FCSTD DOCUMENT  (FreeCAD 1.0R39109 (Git))
Label: 00_tool_cabinet_assembly
License: All rights reserved
LicenseURL: http://en.wikipedia.org/wiki/All_rights_reserved
objects: App::Link×62, App::FeaturePython×28, TechDraw::DrawViewDimension×15, Assembly::AssemblyLink×10, TechDraw::DrawProjGroupItem×5, TechDraw::DrawSVGTemplate×1, Assembly::JointGroup×1, Assembly::AssemblyObject×1, TechDraw::DrawProjGroup×1, TechDraw::DrawViewSection×1, TechDraw::DrawPage×1
note: 26 computed .brp shape members not serialized (recipe doc carries the construction recipe); baked Part::Feature solids carry a one-line shape summary decoded from their .brp
EXTERNAL_REF file=80_base_assembly.FCStd obj=Assembly
EXTERNAL_REF file=80_base_assembly.FCStd obj=Body
EXTERNAL_REF file=80_base_assembly.FCStd obj=Body001
EXTERNAL_REF file=80_base_assembly.FCStd obj=Body002
EXTERNAL_REF file=80_base_assembly.FCStd obj=Body003
EXTERNAL_REF file=10_drawer_96mm_assembly.FCStd obj=Assembly
EXTERNAL_REF file=10_drawer_96mm_assembly.FCStd obj=Body
EXTERNAL_REF file=10_drawer_96mm_assembly.FCStd obj=Body001
EXTERNAL_REF file=10_drawer_96mm_assembly.FCStd obj=Body002
EXTERNAL_REF file=10_drawer_96mm_assembly.FCStd obj=Body003
EXTERNAL_REF file=10_drawer_96mm_assembly.FCStd obj=Body004
EXTERNAL_REF file=10_drawer_96mm_assembly.FCStd obj=Body005
EXTERNAL_REF file=70_drawer_box_assembly.FCStd obj=Assembly
EXTERNAL_REF file=70_drawer_box_assembly.FCStd obj=Body
EXTERNAL_REF file=70_drawer_box_assembly.FCStd obj=Body003
EXTERNAL_REF file=70_drawer_box_assembly.FCStd obj=Body004
EXTERNAL_REF file=70_drawer_box_assembly.FCStd obj=Body005
EXTERNAL_REF file=70_drawer_box_assembly.FCStd obj=KV1_45_H45_L____SC
EXTERNAL_REF file=70_drawer_box_assembly.FCStd obj=Body007
EXTERNAL_REF file=70_drawer_box_assembly.FCStd obj=Assembly001
EXTERNAL_REF file=70_drawer_box_assembly.FCStd obj=KV1_45_H45_L____SC001
EXTERNAL_REF file=70_drawer_box_assembly.FCStd obj=KV1_45_H45_L____SC002
EXTERNAL_REF file=70_drawer_box_assembly.FCStd obj=KV1_45_H45_L____SC003

FEATURE [TechDraw::DrawSVGTemplate] Template
  Height = 210
  Orientation = 1
  Template = C:/Program Files/FreeCAD 1.0/data/Mod/TechDraw/Templates/Default_Template_A4_Landscape.svg
  Width = 297
FEATURE [App::Link] Body
  LinkedObject = -> <external 80_base_assembly.FCStd>#Body
FEATURE [App::Link] Body001
  LinkPlacement = pos=(-1.91e-14,1.232e-13,375) rot=(1,0,0;3.14159rad)
  LinkedObject = -> <external 80_base_assembly.FCStd>#Body001
  Placement = pos=(-1.91e-14,1.232e-13,375) rot=(1,0,0;3.14159rad)
FEATURE [App::Link] Body002
  LinkPlacement = pos=(-262.5,9.58e-14,187.5) rot=(0.707107,0,0.707107;3.14159rad)
  LinkedObject = -> <external 80_base_assembly.FCStd>#Body002
  Placement = pos=(-262.5,9.58e-14,187.5) rot=(0.707107,0,0.707107;3.14159rad)
FEATURE [App::Link] Body003
  LinkPlacement = pos=(244.5,3.53e-14,187.5) rot=(0,1,0;1.5708rad)
  LinkedObject = -> <external 80_base_assembly.FCStd>#Body003
  Placement = pos=(244.5,3.53e-14,187.5) rot=(0,1,0;1.5708rad)
FEATURE [Assembly::AssemblyLink] Assembly001
  Group = -> [Body,Body001,Body002,Body003]
  LinkedObject = -> <external 80_base_assembly.FCStd>#Assembly
  Origin = -> Origin001
  Rigid = true
FEATURE [App::FeaturePython] GroundedJoint  # Assembly grounded joint (typed FeaturePython)
  ObjectToGround = -> Assembly001
FEATURE [App::Link] Body004
  LinkedObject = -> <external 10_drawer_96mm_assembly.FCStd>#Body
FEATURE [App::Link] Body005
  LinkPlacement = pos=(-0.0692255,177.5,34.4999) rot=(0.999999,-0.001116,0.001116;1.5708rad)
  LinkedObject = -> <external 10_drawer_96mm_assembly.FCStd>#Body001
  Placement = pos=(-0.0692255,177.5,34.4999) rot=(0.999999,-0.001116,0.001116;1.5708rad)
FEATURE [App::Link] Body006
  LinkPlacement = pos=(2.3e-15,-177.5,34) rot=(0,0.707107,0.707107;3.14159rad)
  LinkedObject = -> <external 10_drawer_96mm_assembly.FCStd>#Body002
  Placement = pos=(2.3e-15,-177.5,34) rot=(0,0.707107,0.707107;3.14159rad)
FEATURE [App::Link] Body007
  LinkPlacement = pos=(-231.5,-4.06e-14,34) rot=(0.57735,0.57735,0.57735;2.0944rad)
  LinkedObject = -> <external 10_drawer_96mm_assembly.FCStd>#Body003
  Placement = pos=(-231.5,-4.06e-14,34) rot=(0.57735,0.57735,0.57735;2.0944rad)
FEATURE [App::Link] Body008
  LinkPlacement = pos=(231.5,-6.4e-15,34) rot=(0.57735,-0.57735,-0.57735;2.0944rad)
  LinkedObject = -> <external 10_drawer_96mm_assembly.FCStd>#Body004
  Placement = pos=(231.5,-6.4e-15,34) rot=(0.57735,-0.57735,-0.57735;2.0944rad)
FEATURE [App::Link] Body009
  LinkPlacement = pos=(2.5e-15,-177.5,33.5) rot=(0,-0.707107,0.707107;3.14159rad)
  LinkedObject = -> <external 10_drawer_96mm_assembly.FCStd>#Body005
  Placement = pos=(2.5e-15,-177.5,33.5) rot=(0,-0.707107,0.707107;3.14159rad)
FEATURE [Assembly::AssemblyLink] Assembly002
  Group = -> [Body004,Body005,Body006,Body007,Body008,Body009]
  LinkedObject = -> <external 10_drawer_96mm_assembly.FCStd>#Assembly
  Origin = -> Origin002
  Placement = pos=(-8.81e-14,-59,174.5) rot=(1,0,0;1.5708rad)
  Rigid = true
FEATURE [App::Link] Body010
  LinkPlacement = pos=(0,0,0) rot=(0,0,1;3.14159rad)
  LinkedObject = -> <external 70_drawer_box_assembly.FCStd>#Body
  Placement = pos=(0,0,0) rot=(0,0,1;3.14159rad)
FEATURE [App::Link] Body011
  LinkPlacement = pos=(-1.536e-13,-1.625e-13,-771) rot=(1,0,0;3.14159rad)
  LinkedObject = -> <external 70_drawer_box_assembly.FCStd>#Body003
  Placement = pos=(-1.536e-13,-1.625e-13,-771) rot=(1,0,0;3.14159rad)
FEATURE [App::Link] Body012
  LinkPlacement = pos=(-262.5,7.5,-385.5) rot=(0,1,0;1.5708rad)
  LinkedObject = -> <external 70_drawer_box_assembly.FCStd>#Body004
  Placement = pos=(-262.5,7.5,-385.5) rot=(0,1,0;1.5708rad)
FEATURE [App::Link] Body013
  LinkPlacement = pos=(244.5,7.5,-385.5) rot=(0,1,0;1.5708rad)
  LinkedObject = -> <external 70_drawer_box_assembly.FCStd>#Body005
  Placement = pos=(244.5,7.5,-385.5) rot=(0,1,0;1.5708rad)
FEATURE [App::Link] KV1_45_H45_L____SC  label="KV1-45-H45-L...-SC"
  LinkPlacement = pos=(238.45,-31,-41.5) rot=(0,-0.707107,0.707107;3.14159rad)
  LinkedObject = -> <external 70_drawer_box_assembly.FCStd>#KV1_45_H45_L____SC
  Placement = pos=(238.45,-31,-41.5) rot=(0,-0.707107,0.707107;3.14159rad)
FEATURE [App::Link] Body014
  LinkPlacement = pos=(-8.19e-14,196.5,-386) rot=(0,-0.707107,0.707107;3.14159rad)
  LinkedObject = -> <external 70_drawer_box_assembly.FCStd>#Body007
  Placement = pos=(-8.19e-14,196.5,-386) rot=(0,-0.707107,0.707107;3.14159rad)
FEATURE [App::FeaturePython] Joint  label="Distance"  # Assembly joint (typed FeaturePython)
  Activated = true
  AngleMax = 0
  AngleMin = 0
  Detach1 = false
  Detach2 = false
  Distance = 0
  Distance2 = 0
  EnableAngleMax = false
  EnableAngleMin = false
  EnableLengthMax = false
  EnableLengthMin = false
  JointType = 5 (Distance)
  LengthMax = 0
  LengthMin = 0
  Placement1 = pos=(4.7e-15,6.1e-15,18) rot=(0,0,1;0rad)
  Placement2 = pos=(0,25,9) rot=(-1,0,0;1.5708rad)
  Reference1 = -> Assembly [Assembly003.Body010.Face5,Assembly003.Body010.Face5]
  Reference2 = -> Assembly [Assembly001.Body002.Face1,Assembly001.Body002.Vertex3]
FEATURE [App::FeaturePython] Joint001  label="Distance001"  # Assembly joint (typed FeaturePython)
  Activated = true
  AngleMax = 0
  AngleMin = 0
  Detach1 = false
  Detach2 = false
  Distance = 0
  Distance2 = 0
  EnableAngleMax = false
  EnableAngleMin = false
  EnableLengthMax = false
  EnableLengthMin = false
  JointType = 5 (Distance)
  LengthMax = 0
  LengthMin = 0
  Placement1 = pos=(262.5,2.2e-15,9) rot=(-0.57735,0.57735,-0.57735;2.0944rad)
  Placement2 = pos=(0,-3e-16,18) rot=(0,0,1;0rad)
  Reference1 = -> Assembly [Assembly003.Body010.Face3,Assembly003.Body010.Vertex4]
  Reference2 = -> Assembly [Assembly001.Body003.Face6,Assembly001.Body003.Face6]
FEATURE [App::FeaturePython] Joint002  label="Distance002"  # Assembly joint (typed FeaturePython)
  Activated = true
  AngleMax = 0
  AngleMin = 0
  Detach1 = false
  Detach2 = false
  Distance = 0
  Distance2 = 0
  EnableAngleMax = false
  EnableAngleMin = false
  EnableLengthMax = false
  EnableLengthMin = false
  JointType = 5 (Distance)
  LengthMax = 0
  LengthMin = 0
  Placement1 = pos=(-1e-14,0,0) rot=(0,0,1;0rad)
  Placement2 = pos=(-2e-16,-196.5,9) rot=(0,0.707107,-0.707107;3.14159rad)
  Reference1 = -> Assembly [Assembly001.Body001.Face5,Assembly001.Body001.Vertex5]
  Reference2 = -> Assembly [Assembly003.Body010.Face6,Assembly003.Body010.Vertex7]
FEATURE [App::FeaturePython] Joint003  label="Distance003"  # Assembly joint (typed FeaturePython)
  Activated = true
  AngleMax = 0
  AngleMin = 0
  Detach1 = false
  Detach2 = false
  Distance = 3
  Distance2 = 0
  EnableAngleMax = false
  EnableAngleMin = false
  EnableLengthMax = false
  EnableLengthMin = false
  JointType = 5 (Distance)
  LengthMax = 0
  LengthMin = 0
  Placement1 = pos=(-6.6e-15,46.5,7.5) rot=(1,0,0;4.71239rad)
  Placement2 = pos=(4.7e-15,3.01501,0) rot=(0,0,1;0rad)
  Reference1 = -> Assembly [Assembly002.Body009.Face1,Assembly002.Body009.Face1]
  Reference2 = -> Assembly [Assembly003.Body010.Face4,Assembly003.Body010.Face4]
FEATURE [App::FeaturePython] Joint004  label="Distance004"  # Assembly joint (typed FeaturePython)
  Activated = true
  AngleMax = 0
  AngleMin = 0
  Detach1 = false
  Detach2 = false
  Distance = 0
  Distance2 = 0
  EnableAngleMax = false
  EnableAngleMin = false
  EnableLengthMax = false
  EnableLengthMin = false
  JointType = 5 (Distance)
  LengthMax = 0
  LengthMin = 0
  Placement1 = pos=(3.9e-15,0,0) rot=(0,0,1;0rad)
  Placement2 = pos=(0,-189,9) rot=(0,-0.707107,0.707107;3.14159rad)
  Reference1 = -> Assembly [Assembly002.Body009.Face5,Assembly002.Body009.Vertex1]
  Reference2 = -> Assembly [Assembly003.Body012.Face10,Assembly003.Body012.Vertex10]
FEATURE [App::FeaturePython] Joint005  label="Distance005"  # Assembly joint (typed FeaturePython)
  Activated = true
  AngleMax = 0
  AngleMin = 0
  Detach1 = false
  Detach2 = false
  Distance = 2
  Distance2 = 0
  EnableAngleMax = false
  EnableAngleMin = false
  EnableLengthMax = false
  EnableLengthMin = false
  JointType = 5 (Distance)
  LengthMax = 0
  LengthMin = 0
  Placement1 = pos=(260.5,-7.1e-15,7.5) rot=(-0.57735,0.57735,-0.57735;2.0944rad)
  Placement2 = pos=(0,3.6e-15,18) rot=(0,0,1;0rad)
  Reference1 = -> Assembly [Assembly002.Body009.Face2,Assembly002.Body009.Face2]
  Reference2 = -> Assembly [Assembly003.Body013.Face5,Assembly003.Body013.Vertex10]
FEATURE [App::Link] Assembly004
  LinkedObject = -> <external 70_drawer_box_assembly.FCStd>#Assembly001
FEATURE [App::Link] KV1_45_H45_L____SC001  label="KV1-45-H45-L...-SC001"
  LinkPlacement = pos=(239.05,-31,-233.479) rot=(-0.001394,0.707106,-0.707106;3.14438rad)
  LinkedObject = -> <external 70_drawer_box_assembly.FCStd>#KV1_45_H45_L____SC001
  Placement = pos=(239.05,-31,-233.479) rot=(-0.001394,0.707106,-0.707106;3.14438rad)
FEATURE [App::Link] KV1_45_H45_L____SC002  label="KV1-45-H45-L...-SC002"
  LinkPlacement = pos=(238.45,-31,-137.5) rot=(0,-0.707107,0.707107;3.14159rad)
  LinkedObject = -> <external 70_drawer_box_assembly.FCStd>#KV1_45_H45_L____SC002
  Placement = pos=(238.45,-31,-137.5) rot=(0,-0.707107,0.707107;3.14159rad)
FEATURE [App::Link] KV1_45_H45_L____SC003  label="KV1-45-H45-L...-SC003"
  LinkPlacement = pos=(238.71,-31.0451,-329.552) rot=(0.002831,-0.706671,0.707537;3.14726rad)
  LinkedObject = -> <external 70_drawer_box_assembly.FCStd>#KV1_45_H45_L____SC003
  Placement = pos=(238.71,-31.0451,-329.552) rot=(0.002831,-0.706671,0.707537;3.14726rad)
FEATURE [Assembly::AssemblyLink] Assembly003
  Group = -> [Body010,Body011,Body012,Body013,KV1_45_H45_L____SC,Body014,Assembly004,KV1_45_H45_L____SC001,KV1_45_H45_L____SC002,KV1_45_H45_L____SC003]
  LinkedObject = -> <external 70_drawer_box_assembly.FCStd>#Assembly
  Origin = -> Origin003
  Placement = pos=(-1.92e-14,-43,178.5) rot=(0,0.707107,0.707107;3.14159rad)
  Rigid = true
FEATURE [App::Link] Body015
  LinkedObject = -> <external 10_drawer_96mm_assembly.FCStd>#Body
FEATURE [App::Link] Body016
  LinkPlacement = pos=(-0.0692255,177.5,34.4999) rot=(0.999999,-0.001116,0.001116;1.5708rad)
  LinkedObject = -> <external 10_drawer_96mm_assembly.FCStd>#Body001
  Placement = pos=(-0.0692255,177.5,34.4999) rot=(0.999999,-0.001116,0.001116;1.5708rad)
FEATURE [App::Link] Body017
  LinkPlacement = pos=(2.3e-15,-177.5,34) rot=(0,0.707107,0.707107;3.14159rad)
  LinkedObject = -> <external 10_drawer_96mm_assembly.FCStd>#Body002
  Placement = pos=(2.3e-15,-177.5,34) rot=(0,0.707107,0.707107;3.14159rad)
FEATURE [App::Link] Body018
  LinkPlacement = pos=(-231.5,-4.06e-14,34) rot=(0.57735,0.57735,0.57735;2.0944rad)
  LinkedObject = -> <external 10_drawer_96mm_assembly.FCStd>#Body003
  Placement = pos=(-231.5,-4.06e-14,34) rot=(0.57735,0.57735,0.57735;2.0944rad)
FEATURE [App::Link] Body019
  LinkPlacement = pos=(231.5,-6.4e-15,34) rot=(0.57735,-0.57735,-0.57735;2.0944rad)
  LinkedObject = -> <external 10_drawer_96mm_assembly.FCStd>#Body004
  Placement = pos=(231.5,-6.4e-15,34) rot=(0.57735,-0.57735,-0.57735;2.0944rad)
FEATURE [App::Link] Body020
  LinkPlacement = pos=(2.5e-15,-177.5,33.5) rot=(0,-0.707107,0.707107;3.14159rad)
  LinkedObject = -> <external 10_drawer_96mm_assembly.FCStd>#Body005
  Placement = pos=(2.5e-15,-177.5,33.5) rot=(0,-0.707107,0.707107;3.14159rad)
FEATURE [Assembly::AssemblyLink] Assembly005
  Group = -> [Body015,Body016,Body017,Body018,Body019,Body020]
  LinkedObject = -> <external 10_drawer_96mm_assembly.FCStd>#Assembly
  Origin = -> Origin004
  Placement = pos=(-9.65e-14,-155,174.5) rot=(1,0,0;1.5708rad)
  Rigid = true
FEATURE [App::FeaturePython] Joint006  label="Distance006"  # Assembly joint (typed FeaturePython)
  Activated = true
  AngleMax = 0
  AngleMin = 0
  Detach1 = false
  Detach2 = false
  Distance = 3
  Distance2 = 0
  EnableAngleMax = false
  EnableAngleMin = false
  EnableLengthMax = false
  EnableLengthMin = false
  JointType = 5 (Distance)
  LengthMax = 0
  LengthMin = 0
  Placement1 = pos=(-6.6e-15,46.5,7.5) rot=(1,0,0;4.71239rad)
  Placement2 = pos=(1.03e-14,-46.5,7.5) rot=(0,0.707107,-0.707107;3.14159rad)
  Reference1 = -> Assembly [Assembly005.Body020.Face1,Assembly005.Body020.Face1]
  Reference2 = -> Assembly [Assembly002.Body009.Face3,Assembly002.Body009.Vertex5]
FEATURE [App::FeaturePython] Joint007  label="Distance007"  # Assembly joint (typed FeaturePython)
  Activated = true
  AngleMax = 0
  AngleMin = 0
  Detach1 = false
  Detach2 = false
  Distance = 0
  Distance2 = 0
  EnableAngleMax = false
  EnableAngleMin = false
  EnableLengthMax = false
  EnableLengthMin = false
  JointType = 5 (Distance)
  LengthMax = 0
  LengthMin = 0
  Placement1 = pos=(0,-189,9) rot=(0,-0.707107,0.707107;3.14159rad)
  Placement2 = pos=(3.9e-15,0,0) rot=(0,0,1;0rad)
  Reference1 = -> Assembly [Assembly003.Body012.Face10,Assembly003.Body012.Vertex10]
  Reference2 = -> Assembly [Assembly005.Body020.Face5,Assembly005.Body020.Vertex1]
FEATURE [App::FeaturePython] Joint008  label="Distance008"  # Assembly joint (typed FeaturePython)
  Activated = true
  AngleMax = 0
  AngleMin = 0
  Detach1 = false
  Detach2 = false
  Distance = 2
  Distance2 = 0
  EnableAngleMax = false
  EnableAngleMin = false
  EnableLengthMax = false
  EnableLengthMin = false
  JointType = 5 (Distance)
  LengthMax = 0
  LengthMin = 0
  Placement1 = pos=(-260.5,0,7.5) rot=(0.57735,0.57735,-0.57735;4.18879rad)
  Placement2 = pos=(0,-4.4e-15,0) rot=(0,0,1;0rad)
  Reference1 = -> Assembly [Assembly005.Body020.Face4,Assembly005.Body020.Face4]
  Reference2 = -> Assembly [Assembly003.Body012.Face4,Assembly003.Body012.Vertex5]
FEATURE [App::Link] Body021
  LinkedObject = -> <external 10_drawer_96mm_assembly.FCStd>#Body
FEATURE [App::Link] Body022
  LinkPlacement = pos=(-0.0692255,177.5,34.4999) rot=(0.999999,-0.001116,0.001116;1.5708rad)
  LinkedObject = -> <external 10_drawer_96mm_assembly.FCStd>#Body001
  Placement = pos=(-0.0692255,177.5,34.4999) rot=(0.999999,-0.001116,0.001116;1.5708rad)
FEATURE [App::Link] Body023
  LinkPlacement = pos=(2.3e-15,-177.5,34) rot=(0,0.707107,0.707107;3.14159rad)
  LinkedObject = -> <external 10_drawer_96mm_assembly.FCStd>#Body002
  Placement = pos=(2.3e-15,-177.5,34) rot=(0,0.707107,0.707107;3.14159rad)
FEATURE [App::Link] Body024
  LinkPlacement = pos=(-231.5,-4.06e-14,34) rot=(0.57735,0.57735,0.57735;2.0944rad)
  LinkedObject = -> <external 10_drawer_96mm_assembly.FCStd>#Body003
  Placement = pos=(-231.5,-4.06e-14,34) rot=(0.57735,0.57735,0.57735;2.0944rad)
FEATURE [App::Link] Body025
  LinkPlacement = pos=(231.5,-6.4e-15,34) rot=(0.57735,-0.57735,-0.57735;2.0944rad)
  LinkedObject = -> <external 10_drawer_96mm_assembly.FCStd>#Body004
  Placement = pos=(231.5,-6.4e-15,34) rot=(0.57735,-0.57735,-0.57735;2.0944rad)
FEATURE [App::Link] Body026
  LinkPlacement = pos=(2.5e-15,-177.5,33.5) rot=(0,-0.707107,0.707107;3.14159rad)
  LinkedObject = -> <external 10_drawer_96mm_assembly.FCStd>#Body005
  Placement = pos=(2.5e-15,-177.5,33.5) rot=(0,-0.707107,0.707107;3.14159rad)
FEATURE [Assembly::AssemblyLink] Assembly006
  Group = -> [Body021,Body022,Body023,Body024,Body025,Body026]
  LinkedObject = -> <external 10_drawer_96mm_assembly.FCStd>#Assembly
  Origin = -> Origin005
  Placement = pos=(2.04e-14,-347,174.5) rot=(1,0,0;1.5708rad)
  Rigid = true
FEATURE [App::Link] Body027
  LinkedObject = -> <external 10_drawer_96mm_assembly.FCStd>#Body
FEATURE [App::Link] Body028
  LinkPlacement = pos=(-0.0692255,177.5,34.4999) rot=(0.999999,-0.001116,0.001116;1.5708rad)
  LinkedObject = -> <external 10_drawer_96mm_assembly.FCStd>#Body001
  Placement = pos=(-0.0692255,177.5,34.4999) rot=(0.999999,-0.001116,0.001116;1.5708rad)
FEATURE [App::Link] Body029
  LinkPlacement = pos=(2.3e-15,-177.5,34) rot=(0,0.707107,0.707107;3.14159rad)
  LinkedObject = -> <external 10_drawer_96mm_assembly.FCStd>#Body002
  Placement = pos=(2.3e-15,-177.5,34) rot=(0,0.707107,0.707107;3.14159rad)
FEATURE [App::Link] Body030
  LinkPlacement = pos=(-231.5,-4.06e-14,34) rot=(0.57735,0.57735,0.57735;2.0944rad)
  LinkedObject = -> <external 10_drawer_96mm_assembly.FCStd>#Body003
  Placement = pos=(-231.5,-4.06e-14,34) rot=(0.57735,0.57735,0.57735;2.0944rad)
FEATURE [App::Link] Body031
  LinkPlacement = pos=(231.5,-6.4e-15,34) rot=(0.57735,-0.57735,-0.57735;2.0944rad)
  LinkedObject = -> <external 10_drawer_96mm_assembly.FCStd>#Body004
  Placement = pos=(231.5,-6.4e-15,34) rot=(0.57735,-0.57735,-0.57735;2.0944rad)
FEATURE [App::Link] Body032
  LinkPlacement = pos=(2.5e-15,-177.5,33.5) rot=(0,-0.707107,0.707107;3.14159rad)
  LinkedObject = -> <external 10_drawer_96mm_assembly.FCStd>#Body005
  Placement = pos=(2.5e-15,-177.5,33.5) rot=(0,-0.707107,0.707107;3.14159rad)
FEATURE [Assembly::AssemblyLink] Assembly007
  Group = -> [Body027,Body028,Body029,Body030,Body031,Body032]
  LinkedObject = -> <external 10_drawer_96mm_assembly.FCStd>#Assembly
  Origin = -> Origin006
  Placement = pos=(3.41e-14,-251,174.5) rot=(1,0,0;1.5708rad)
  Rigid = true
FEATURE [App::FeaturePython] Joint009  label="Distance009"  # Assembly joint (typed FeaturePython)
  Activated = true
  AngleMax = 0
  AngleMin = 0
  Detach1 = false
  Detach2 = false
  Distance = 3
  Distance2 = 0
  EnableAngleMax = false
  EnableAngleMin = false
  EnableLengthMax = false
  EnableLengthMin = false
  JointType = 5 (Distance)
  LengthMax = 0
  LengthMin = 0
  Placement1 = pos=(-6.6e-15,46.5,7.5) rot=(1,0,0;4.71239rad)
  Placement2 = pos=(1.03e-14,-46.5,7.5) rot=(0,0.707107,-0.707107;3.14159rad)
  Reference1 = -> Assembly [Assembly007.Body032.Face1,Assembly007.Body032.Vertex3]
  Reference2 = -> Assembly [Assembly005.Body020.Face3,Assembly005.Body020.Face3]
FEATURE [App::FeaturePython] Joint010  label="Distance010"  # Assembly joint (typed FeaturePython)
  Activated = true
  AngleMax = 0
  AngleMin = 0
  Detach1 = false
  Detach2 = false
  Distance = 0
  Distance2 = 0
  EnableAngleMax = false
  EnableAngleMin = false
  EnableLengthMax = false
  EnableLengthMin = false
  JointType = 5 (Distance)
  LengthMax = 0
  LengthMin = 0
  Placement1 = pos=(0,-189,9) rot=(0,-0.707107,0.707107;3.14159rad)
  Placement2 = pos=(3.9e-15,0,0) rot=(0,0,1;0rad)
  Reference1 = -> Assembly [Assembly003.Body012.Face10,Assembly003.Body012.Face10]
  Reference2 = -> Assembly [Assembly007.Body032.Face5,Assembly007.Body032.Vertex7]
FEATURE [App::FeaturePython] Joint011  label="Distance011"  # Assembly joint (typed FeaturePython)
  Activated = true
  AngleMax = 0
  AngleMin = 0
  Detach1 = false
  Detach2 = false
  Distance = 2
  Distance2 = 0
  EnableAngleMax = false
  EnableAngleMin = false
  EnableLengthMax = false
  EnableLengthMin = false
  JointType = 5 (Distance)
  LengthMax = 0
  LengthMin = 0
  Placement1 = pos=(-260.5,0,7.5) rot=(0.57735,0.57735,-0.57735;4.18879rad)
  Placement2 = pos=(0,-4.4e-15,0) rot=(0,0,1;0rad)
  Reference1 = -> Assembly [Assembly007.Body032.Face4,Assembly007.Body032.Face4]
  Reference2 = -> Assembly [Assembly003.Body012.Face4,Assembly003.Body012.Face4]
FEATURE [App::FeaturePython] Joint012  label="Distance012"  # Assembly joint (typed FeaturePython)
  Activated = true
  AngleMax = 0
  AngleMin = 0
  Detach1 = false
  Detach2 = false
  Distance = 3
  Distance2 = 0
  EnableAngleMax = false
  EnableAngleMin = false
  EnableLengthMax = false
  EnableLengthMin = false
  JointType = 5 (Distance)
  LengthMax = 0
  LengthMin = 0
  Placement1 = pos=(-6.6e-15,46.5,7.5) rot=(1,0,0;4.71239rad)
  Placement2 = pos=(1.03e-14,-46.5,7.5) rot=(0,0.707107,-0.707107;3.14159rad)
  Reference1 = -> Assembly [Assembly006.Body026.Face1,Assembly006.Body026.Vertex1]
  Reference2 = -> Assembly [Assembly007.Body032.Face3,Assembly007.Body032.Face3]
FEATURE [App::FeaturePython] Joint013  label="Distance013"  # Assembly joint (typed FeaturePython)
  Activated = true
  AngleMax = 0
  AngleMin = 0
  Detach1 = false
  Detach2 = false
  Distance = 0
  Distance2 = 0
  EnableAngleMax = false
  EnableAngleMin = false
  EnableLengthMax = false
  EnableLengthMin = false
  JointType = 5 (Distance)
  LengthMax = 0
  LengthMin = 0
  Placement1 = pos=(3.9e-15,0,0) rot=(0,0,1;0rad)
  Placement2 = pos=(0,-189,9) rot=(0,-0.707107,0.707107;3.14159rad)
  Reference1 = -> Assembly [Assembly006.Body026.Face5,Assembly006.Body026.Vertex1]
  Reference2 = -> Assembly [Assembly003.Body012.Face10,Assembly003.Body012.Face10]
FEATURE [App::FeaturePython] Joint014  label="Distance014"  # Assembly joint (typed FeaturePython)
  Activated = true
  AngleMax = 0
  AngleMin = 0
  Detach1 = false
  Detach2 = false
  Distance = 2
  Distance2 = 0
  EnableAngleMax = false
  EnableAngleMin = false
  EnableLengthMax = false
  EnableLengthMin = false
  JointType = 5 (Distance)
  LengthMax = 0
  LengthMin = 0
  Placement1 = pos=(-260.5,0,7.5) rot=(0.57735,0.57735,-0.57735;4.18879rad)
  Placement2 = pos=(0,-4.4e-15,0) rot=(0,0,1;0rad)
  Reference1 = -> Assembly [Assembly006.Body026.Face4,Assembly006.Body026.Face4]
  Reference2 = -> Assembly [Assembly003.Body012.Face4,Assembly003.Body012.Face4]
FEATURE [App::Link] Body033
  LinkedObject = -> <external 10_drawer_96mm_assembly.FCStd>#Body
FEATURE [App::Link] Body034
  LinkPlacement = pos=(-0.0692255,177.5,34.4999) rot=(0.999999,-0.001116,0.001116;1.5708rad)
  LinkedObject = -> <external 10_drawer_96mm_assembly.FCStd>#Body001
  Placement = pos=(-0.0692255,177.5,34.4999) rot=(0.999999,-0.001116,0.001116;1.5708rad)
FEATURE [App::Link] Body035
  LinkPlacement = pos=(2.3e-15,-177.5,34) rot=(0,0.707107,0.707107;3.14159rad)
  LinkedObject = -> <external 10_drawer_96mm_assembly.FCStd>#Body002
  Placement = pos=(2.3e-15,-177.5,34) rot=(0,0.707107,0.707107;3.14159rad)
FEATURE [App::Link] Body036
  LinkPlacement = pos=(-231.5,-4.06e-14,34) rot=(0.57735,0.57735,0.57735;2.0944rad)
  LinkedObject = -> <external 10_drawer_96mm_assembly.FCStd>#Body003
  Placement = pos=(-231.5,-4.06e-14,34) rot=(0.57735,0.57735,0.57735;2.0944rad)
FEATURE [App::Link] Body037
  LinkPlacement = pos=(231.5,-6.4e-15,34) rot=(0.57735,-0.57735,-0.57735;2.0944rad)
  LinkedObject = -> <external 10_drawer_96mm_assembly.FCStd>#Body004
  Placement = pos=(231.5,-6.4e-15,34) rot=(0.57735,-0.57735,-0.57735;2.0944rad)
FEATURE [App::Link] Body038
  LinkPlacement = pos=(2.5e-15,-177.5,33.5) rot=(0,-0.707107,0.707107;3.14159rad)
  LinkedObject = -> <external 10_drawer_96mm_assembly.FCStd>#Body005
  Placement = pos=(2.5e-15,-177.5,33.5) rot=(0,-0.707107,0.707107;3.14159rad)
FEATURE [Assembly::AssemblyLink] Assembly008
  Group = -> [Body033,Body034,Body035,Body036,Body037,Body038]
  LinkedObject = -> <external 10_drawer_96mm_assembly.FCStd>#Assembly
  Origin = -> Origin007
  Placement = pos=(3.815e-13,-731,174.5) rot=(1,0,0;1.5708rad)
  Rigid = true
FEATURE [App::Link] Body039
  LinkedObject = -> <external 10_drawer_96mm_assembly.FCStd>#Body
FEATURE [App::Link] Body040
  LinkPlacement = pos=(-0.0692255,177.5,34.4999) rot=(0.999999,-0.001116,0.001116;1.5708rad)
  LinkedObject = -> <external 10_drawer_96mm_assembly.FCStd>#Body001
  Placement = pos=(-0.0692255,177.5,34.4999) rot=(0.999999,-0.001116,0.001116;1.5708rad)
FEATURE [App::Link] Body041
  LinkPlacement = pos=(2.3e-15,-177.5,34) rot=(0,0.707107,0.707107;3.14159rad)
  LinkedObject = -> <external 10_drawer_96mm_assembly.FCStd>#Body002
  Placement = pos=(2.3e-15,-177.5,34) rot=(0,0.707107,0.707107;3.14159rad)
FEATURE [App::Link] Body042
  LinkPlacement = pos=(-231.5,-4.06e-14,34) rot=(0.57735,0.57735,0.57735;2.0944rad)
  LinkedObject = -> <external 10_drawer_96mm_assembly.FCStd>#Body003
  Placement = pos=(-231.5,-4.06e-14,34) rot=(0.57735,0.57735,0.57735;2.0944rad)
FEATURE [App::Link] Body043
  LinkPlacement = pos=(231.5,-6.4e-15,34) rot=(0.57735,-0.57735,-0.57735;2.0944rad)
  LinkedObject = -> <external 10_drawer_96mm_assembly.FCStd>#Body004
  Placement = pos=(231.5,-6.4e-15,34) rot=(0.57735,-0.57735,-0.57735;2.0944rad)
FEATURE [App::Link] Body044
  LinkPlacement = pos=(2.5e-15,-177.5,33.5) rot=(0,-0.707107,0.707107;3.14159rad)
  LinkedObject = -> <external 10_drawer_96mm_assembly.FCStd>#Body005
  Placement = pos=(2.5e-15,-177.5,33.5) rot=(0,-0.707107,0.707107;3.14159rad)
FEATURE [Assembly::AssemblyLink] Assembly009
  Group = -> [Body039,Body040,Body041,Body042,Body043,Body044]
  LinkedObject = -> <external 10_drawer_96mm_assembly.FCStd>#Assembly
  Origin = -> Origin008
  Placement = pos=(3.911e-13,-635,174.5) rot=(1,0,0;1.5708rad)
  Rigid = true
FEATURE [App::Link] Body045
  LinkedObject = -> <external 10_drawer_96mm_assembly.FCStd>#Body
FEATURE [App::Link] Body046
  LinkPlacement = pos=(-0.0692255,177.5,34.4999) rot=(0.999999,-0.001116,0.001116;1.5708rad)
  LinkedObject = -> <external 10_drawer_96mm_assembly.FCStd>#Body001
  Placement = pos=(-0.0692255,177.5,34.4999) rot=(0.999999,-0.001116,0.001116;1.5708rad)
FEATURE [App::Link] Body047
  LinkPlacement = pos=(2.3e-15,-177.5,34) rot=(0,0.707107,0.707107;3.14159rad)
  LinkedObject = -> <external 10_drawer_96mm_assembly.FCStd>#Body002
  Placement = pos=(2.3e-15,-177.5,34) rot=(0,0.707107,0.707107;3.14159rad)
FEATURE [App::Link] Body048
  LinkPlacement = pos=(-231.5,-4.06e-14,34) rot=(0.57735,0.57735,0.57735;2.0944rad)
  LinkedObject = -> <external 10_drawer_96mm_assembly.FCStd>#Body003
  Placement = pos=(-231.5,-4.06e-14,34) rot=(0.57735,0.57735,0.57735;2.0944rad)
FEATURE [App::Link] Body049
  LinkPlacement = pos=(231.5,-6.4e-15,34) rot=(0.57735,-0.57735,-0.57735;2.0944rad)
  LinkedObject = -> <external 10_drawer_96mm_assembly.FCStd>#Body004
  Placement = pos=(231.5,-6.4e-15,34) rot=(0.57735,-0.57735,-0.57735;2.0944rad)
FEATURE [App::Link] Body050
  LinkPlacement = pos=(2.5e-15,-177.5,33.5) rot=(0,-0.707107,0.707107;3.14159rad)
  LinkedObject = -> <external 10_drawer_96mm_assembly.FCStd>#Body005
  Placement = pos=(2.5e-15,-177.5,33.5) rot=(0,-0.707107,0.707107;3.14159rad)
FEATURE [Assembly::AssemblyLink] Assembly010
  Group = -> [Body045,Body046,Body047,Body048,Body049,Body050]
  LinkedObject = -> <external 10_drawer_96mm_assembly.FCStd>#Assembly
  Origin = -> Origin009
  Placement = pos=(7.7e-15,-443,174.5) rot=(1,0,0;1.5708rad)
  Rigid = true
FEATURE [App::Link] Body051
  LinkedObject = -> <external 10_drawer_96mm_assembly.FCStd>#Body
FEATURE [App::Link] Body052
  LinkPlacement = pos=(-0.0692255,177.5,34.4999) rot=(0.999999,-0.001116,0.001116;1.5708rad)
  LinkedObject = -> <external 10_drawer_96mm_assembly.FCStd>#Body001
  Placement = pos=(-0.0692255,177.5,34.4999) rot=(0.999999,-0.001116,0.001116;1.5708rad)
FEATURE [App::Link] Body053
  LinkPlacement = pos=(2.3e-15,-177.5,34) rot=(0,0.707107,0.707107;3.14159rad)
  LinkedObject = -> <external 10_drawer_96mm_assembly.FCStd>#Body002
  Placement = pos=(2.3e-15,-177.5,34) rot=(0,0.707107,0.707107;3.14159rad)
FEATURE [App::Link] Body054
  LinkPlacement = pos=(-231.5,-4.06e-14,34) rot=(0.57735,0.57735,0.57735;2.0944rad)
  LinkedObject = -> <external 10_drawer_96mm_assembly.FCStd>#Body003
  Placement = pos=(-231.5,-4.06e-14,34) rot=(0.57735,0.57735,0.57735;2.0944rad)
FEATURE [App::Link] Body055
  LinkPlacement = pos=(231.5,-6.4e-15,34) rot=(0.57735,-0.57735,-0.57735;2.0944rad)
  LinkedObject = -> <external 10_drawer_96mm_assembly.FCStd>#Body004
  Placement = pos=(231.5,-6.4e-15,34) rot=(0.57735,-0.57735,-0.57735;2.0944rad)
FEATURE [App::Link] Body056
  LinkPlacement = pos=(2.5e-15,-177.5,33.5) rot=(0,-0.707107,0.707107;3.14159rad)
  LinkedObject = -> <external 10_drawer_96mm_assembly.FCStd>#Body005
  Placement = pos=(2.5e-15,-177.5,33.5) rot=(0,-0.707107,0.707107;3.14159rad)
FEATURE [Assembly::AssemblyLink] Assembly011
  Group = -> [Body051,Body052,Body053,Body054,Body055,Body056]
  LinkedObject = -> <external 10_drawer_96mm_assembly.FCStd>#Assembly
  Origin = -> Origin010
  Placement = pos=(2.778e-13,-539,174.5) rot=(1,0,0;1.5708rad)
  Rigid = true
FEATURE [App::FeaturePython] Joint015  label="Distance015"  # Assembly joint (typed FeaturePython)
  Activated = true
  AngleMax = 0
  AngleMin = 0
  Detach1 = false
  Detach2 = false
  Distance = 3
  Distance2 = 0
  EnableAngleMax = false
  EnableAngleMin = false
  EnableLengthMax = false
  EnableLengthMin = false
  JointType = 5 (Distance)
  LengthMax = 0
  LengthMin = 0
  Placement1 = pos=(-6.6e-15,46.5,7.5) rot=(1,0,0;4.71239rad)
  Placement2 = pos=(1.03e-14,-46.5,7.5) rot=(0,0.707107,-0.707107;3.14159rad)
  Reference1 = -> Assembly [Assembly010.Body050.Face1,Assembly010.Body050.Face1]
  Reference2 = -> Assembly [Assembly006.Body026.Face3,Assembly006.Body026.Vertex7]
FEATURE [App::FeaturePython] Joint016  label="Distance016"  # Assembly joint (typed FeaturePython)
  Activated = true
  AngleMax = 0
  AngleMin = 0
  Detach1 = false
  Detach2 = false
  Distance = 2
  Distance2 = 0
  EnableAngleMax = false
  EnableAngleMin = false
  EnableLengthMax = false
  EnableLengthMin = false
  JointType = 5 (Distance)
  LengthMax = 0
  LengthMin = 0
  Placement1 = pos=(260.5,-7.1e-15,7.5) rot=(-0.57735,0.57735,-0.57735;2.0944rad)
  Placement2 = pos=(0,3.6e-15,18) rot=(0,0,1;0rad)
  Reference1 = -> Assembly [Assembly010.Body050.Face2,Assembly010.Body050.Face2]
  Reference2 = -> Assembly [Assembly003.Body013.Face5,Assembly003.Body013.Face5]
FEATURE [App::FeaturePython] Joint017  label="Distance017"  # Assembly joint (typed FeaturePython)
  Activated = true
  AngleMax = 0
  AngleMin = 0
  Detach1 = false
  Detach2 = false
  Distance = 0
  Distance2 = 0
  EnableAngleMax = false
  EnableAngleMin = false
  EnableLengthMax = false
  EnableLengthMin = false
  JointType = 5 (Distance)
  LengthMax = 0
  LengthMin = 0
  Placement1 = pos=(0,-189,9) rot=(0,-0.707107,0.707107;3.14159rad)
  Placement2 = pos=(3.9e-15,0,0) rot=(0,0,1;0rad)
  Reference1 = -> Assembly [Assembly003.Body013.Face10,Assembly003.Body013.Face10]
  Reference2 = -> Assembly [Assembly010.Body050.Face5,Assembly010.Body050.Vertex5]
FEATURE [App::FeaturePython] Joint018  label="Distance018"  # Assembly joint (typed FeaturePython)
  Activated = true
  AngleMax = 0
  AngleMin = 0
  Detach1 = false
  Detach2 = false
  Distance = 0
  Distance2 = 0
  EnableAngleMax = false
  EnableAngleMin = false
  EnableLengthMax = false
  EnableLengthMin = false
  JointType = 5 (Distance)
  LengthMax = 0
  LengthMin = 0
  Placement1 = pos=(3.9e-15,0,0) rot=(0,0,1;0rad)
  Placement2 = pos=(0,-189,9) rot=(0,-0.707107,0.707107;3.14159rad)
  Reference1 = -> Assembly [Assembly011.Body056.Face5,Assembly011.Body056.Vertex7]
  Reference2 = -> Assembly [Assembly003.Body012.Face10,Assembly003.Body012.Vertex12]
FEATURE [App::FeaturePython] Joint019  label="Distance019"  # Assembly joint (typed FeaturePython)
  Activated = true
  AngleMax = 0
  AngleMin = 0
  Detach1 = false
  Detach2 = false
  Distance = 3
  Distance2 = 0
  EnableAngleMax = false
  EnableAngleMin = false
  EnableLengthMax = false
  EnableLengthMin = false
  JointType = 5 (Distance)
  LengthMax = 0
  LengthMin = 0
  Placement1 = pos=(-6.6e-15,46.5,7.5) rot=(1,0,0;4.71239rad)
  Placement2 = pos=(1.03e-14,-46.5,7.5) rot=(0,0.707107,-0.707107;3.14159rad)
  Reference1 = -> Assembly [Assembly011.Body056.Face1,Assembly011.Body056.Vertex2]
  Reference2 = -> Assembly [Assembly010.Body050.Face3,Assembly010.Body050.Vertex8]
FEATURE [App::FeaturePython] Joint020  label="Distance020"  # Assembly joint (typed FeaturePython)
  Activated = true
  AngleMax = 0
  AngleMin = 0
  Detach1 = false
  Detach2 = false
  Distance = 2
  Distance2 = 0
  EnableAngleMax = false
  EnableAngleMin = false
  EnableLengthMax = false
  EnableLengthMin = false
  JointType = 5 (Distance)
  LengthMax = 0
  LengthMin = 0
  Placement1 = pos=(-260.5,0,7.5) rot=(0.57735,0.57735,-0.57735;4.18879rad)
  Placement2 = pos=(0,-4.4e-15,0) rot=(0,0,1;0rad)
  Reference1 = -> Assembly [Assembly011.Body056.Face4,Assembly011.Body056.Face4]
  Reference2 = -> Assembly [Assembly003.Body012.Face4,Assembly003.Body012.Face4]
FEATURE [App::FeaturePython] Joint021  label="Distance021"  # Assembly joint (typed FeaturePython)
  Activated = true
  AngleMax = 0
  AngleMin = 0
  Detach1 = false
  Detach2 = false
  Distance = 3
  Distance2 = 0
  EnableAngleMax = false
  EnableAngleMin = false
  EnableLengthMax = false
  EnableLengthMin = false
  JointType = 5 (Distance)
  LengthMax = 0
  LengthMin = 0
  Placement1 = pos=(-6.6e-15,46.5,7.5) rot=(1,0,0;4.71239rad)
  Placement2 = pos=(1.03e-14,-46.5,7.5) rot=(0,0.707107,-0.707107;3.14159rad)
  Reference1 = -> Assembly [Assembly009.Body044.Face1,Assembly009.Body044.Face1]
  Reference2 = -> Assembly [Assembly011.Body056.Face3,Assembly011.Body056.Vertex8]
FEATURE [App::FeaturePython] Joint022  label="Distance022"  # Assembly joint (typed FeaturePython)
  Activated = true
  AngleMax = 0
  AngleMin = 0
  Detach1 = false
  Detach2 = false
  Distance = 0
  Distance2 = 0
  EnableAngleMax = false
  EnableAngleMin = false
  EnableLengthMax = false
  EnableLengthMin = false
  JointType = 5 (Distance)
  LengthMax = 0
  LengthMin = 0
  Placement1 = pos=(3.9e-15,0,0) rot=(0,0,1;0rad)
  Placement2 = pos=(0,-189,9) rot=(0,-0.707107,0.707107;3.14159rad)
  Reference1 = -> Assembly [Assembly009.Body044.Face5,Assembly009.Body044.Vertex1]
  Reference2 = -> Assembly [Assembly003.Body012.Face10,Assembly003.Body012.Vertex12]
FEATURE [App::FeaturePython] Joint023  label="Distance023"  # Assembly joint (typed FeaturePython)
  Activated = true
  AngleMax = 0
  AngleMin = 0
  Detach1 = false
  Detach2 = false
  Distance = 2
  Distance2 = 0
  EnableAngleMax = false
  EnableAngleMin = false
  EnableLengthMax = false
  EnableLengthMin = false
  JointType = 5 (Distance)
  LengthMax = 0
  LengthMin = 0
  Placement1 = pos=(-260.5,0,7.5) rot=(0.57735,0.57735,-0.57735;4.18879rad)
  Placement2 = pos=(0,-4.4e-15,0) rot=(0,0,1;0rad)
  Reference1 = -> Assembly [Assembly009.Body044.Face4,Assembly009.Body044.Face4]
  Reference2 = -> Assembly [Assembly003.Body012.Face4,Assembly003.Body012.Vertex11]
FEATURE [App::FeaturePython] Joint024  label="Distance024"  # Assembly joint (typed FeaturePython)
  Activated = true
  AngleMax = 0
  AngleMin = 0
  Detach1 = false
  Detach2 = false
  Distance = 3
  Distance2 = 0
  EnableAngleMax = false
  EnableAngleMin = false
  EnableLengthMax = false
  EnableLengthMin = false
  JointType = 5 (Distance)
  LengthMax = 0
  LengthMin = 0
  Placement1 = pos=(-6.6e-15,46.5,7.5) rot=(1,0,0;4.71239rad)
  Placement2 = pos=(1.03e-14,-46.5,7.5) rot=(0,0.707107,-0.707107;3.14159rad)
  Reference1 = -> Assembly [Assembly008.Body038.Face1,Assembly008.Body038.Vertex3]
  Reference2 = -> Assembly [Assembly009.Body044.Face3,Assembly009.Body044.Face3]
FEATURE [App::FeaturePython] Joint025  label="Distance025"  # Assembly joint (typed FeaturePython)
  Activated = true
  AngleMax = 0
  AngleMin = 0
  Detach1 = false
  Detach2 = false
  Distance = 2
  Distance2 = 0
  EnableAngleMax = false
  EnableAngleMin = false
  EnableLengthMax = false
  EnableLengthMin = false
  JointType = 5 (Distance)
  LengthMax = 0
  LengthMin = 0
  Placement1 = pos=(-260.5,0,7.5) rot=(0.57735,0.57735,-0.57735;4.18879rad)
  Placement2 = pos=(0,-4.4e-15,0) rot=(0,0,1;0rad)
  Reference1 = -> Assembly [Assembly008.Body038.Face4,Assembly008.Body038.Face4]
  Reference2 = -> Assembly [Assembly003.Body012.Face4,Assembly003.Body012.Vertex11]
FEATURE [App::FeaturePython] Joint026  label="Distance026"  # Assembly joint (typed FeaturePython)
  Activated = true
  AngleMax = 0
  AngleMin = 0
  Detach1 = false
  Detach2 = false
  Distance = 0
  Distance2 = 0
  EnableAngleMax = false
  EnableAngleMin = false
  EnableLengthMax = false
  EnableLengthMin = false
  JointType = 5 (Distance)
  LengthMax = 0
  LengthMin = 0
  Placement1 = pos=(3.9e-15,0,0) rot=(0,0,1;0rad)
  Placement2 = pos=(0,-189,9) rot=(0,-0.707107,0.707107;3.14159rad)
  Reference1 = -> Assembly [Assembly008.Body038.Face5,Assembly008.Body038.Vertex7]
  Reference2 = -> Assembly [Assembly003.Body012.Face10,Assembly003.Body012.Vertex11]
FEATURE [Assembly::JointGroup] Joints
  Group = -> [GroundedJoint,Joint,Joint001,Joint002,Joint003,Joint004,Joint005,Joint006,Joint007,Joint008,Joint009,Joint010,Joint011,Joint012,Joint013,Joint014,Joint015,Joint016,Joint017,Joint018,Joint019,Joint020,Joint021,Joint022,Joint023,Joint024,Joint025,Joint026]
FEATURE [Assembly::AssemblyObject] Assembly
  Group = -> [Joints,Assembly001,GroundedJoint,Assembly002,Assembly003,Joint,Joint001,Joint002,Joint003,Joint004,Joint005,Assembly005,Joint006,Joint007,Joint008,Assembly006,Assembly007,Joint009,Joint010,Joint011,Joint012,Joint013,Joint014,Assembly008,Assembly009,Assembly010,Assembly011,Joint015,Joint016,Joint017,Joint018,Joint019,Joint020,Joint021,Joint022,Joint023,Joint024,Joint025,Joint026]
  Origin = -> Origin
  Type = Assembly
FEATURE [TechDraw::DrawProjGroupItem] View  label="Front"
  CoarseView = false
  Direction = (0,-1,0)
  Focus = 100
  HardHidden = false
  IsoCount = 0
  IsoHidden = false
  IsoVisible = false
  LockPosition = true
  Perspective = false
  Rotation = 0
  RotationVector = (1,0,0)
  Scale = 0.2
  ScaleType = 2
  ScrubCount = 1
  SeamHidden = false
  SeamVisible = true
  SmoothHidden = false
  SmoothVisible = true
  Source = -> [Assembly]
  Type = 0
  X = 0
  XDirection = (1,0,0)
  Y = 0
FEATURE [TechDraw::DrawProjGroupItem] ProjItem  label="Left"
  CoarseView = false
  Direction = (-1,-1e-16,0)
  Focus = 100
  HardHidden = false
  IsoCount = 0
  IsoHidden = false
  IsoVisible = false
  LockPosition = false
  Perspective = false
  Rotation = 0
  RotationVector = (1,0,0)
  Scale = 0.2
  ScaleType = 2
  ScrubCount = 1
  SeamHidden = false
  SeamVisible = true
  SmoothHidden = false
  SmoothVisible = true
  Source = -> [Assembly]
  Type = 1
  X = 153.2
  XDirection = (1e-16,-1,0)
  Y = 0
FEATURE [TechDraw::DrawProjGroupItem] ProjItem001  label="Right"
  CoarseView = false
  Direction = (1,-1e-16,0)
  Focus = 100
  HardHidden = false
  IsoCount = 0
  IsoHidden = false
  IsoVisible = false
  LockPosition = false
  Perspective = false
  Rotation = 0
  RotationVector = (1,0,0)
  Scale = 0.2
  ScaleType = 2
  ScrubCount = 1
  SeamHidden = false
  SeamVisible = true
  SmoothHidden = false
  SmoothVisible = true
  Source = -> [Assembly]
  Type = 2
  X = -153.2
  XDirection = (1e-16,1,0)
  Y = 0
FEATURE [TechDraw::DrawProjGroupItem] ProjItem002  label="Top"
  CoarseView = false
  Direction = (0,0,1)
  Focus = 100
  HardHidden = false
  IsoCount = 0
  IsoHidden = false
  IsoVisible = false
  LockPosition = false
  Perspective = false
  Rotation = 0
  RotationVector = (1,0,0)
  ScaleType = 0
  ScrubCount = 1
  SeamHidden = false
  SeamVisible = true
  SmoothHidden = false
  SmoothVisible = true
  Source = -> [Assembly]
  Type = 4
  X = 0
  XDirection = (1,0,0)
  Y = -140
FEATURE [TechDraw::DrawProjGroupItem] ProjItem003  label="Bottom"
  CoarseView = false
  Direction = (0,0,-1)
  Focus = 100
  HardHidden = false
  IsoCount = 0
  IsoHidden = false
  IsoVisible = false
  LockPosition = false
  Perspective = false
  Rotation = 0
  RotationVector = (1,0,0)
  ScaleType = 0
  ScrubCount = 1
  SeamHidden = false
  SeamVisible = true
  SmoothHidden = false
  SmoothVisible = true
  Source = -> [Assembly]
  Type = 5
  X = 0
  XDirection = (1,0,0)
  Y = 140
FEATURE [TechDraw::DrawProjGroup] ProjGroup
  Anchor = -> View
  AutoDistribute = true
  LockPosition = false
  ProjectionType = 0
  Rotation = 0
  Scale = 0.2
  ScaleType = 2
  Source = -> [Assembly]
  Views = -> [View,ProjItem,ProjItem001,ProjItem002,ProjItem003]
  X = 148.5
  Y = 105
  spacingX = 15
  spacingY = 15
FEATURE [TechDraw::DrawViewSection] SectionView  label="Section  - "
  BaseView = -> View
  CoarseView = false
  CutSurfaceDisplay = 2
  Direction = (-1,0,-1e-16)
  FileGeomPattern = <path>\data\Mod/TechDraw/PAT/FCPAT.pat
  FileHatchPattern = <path>\data\Mod/TechDraw/Patterns/simple.svg
  Focus = 100
  FuseBeforeCut = false
  HardHidden = false
  HatchOffset = (0,0,0)
  HatchRotation = 0
  HatchScale = 1
  IsoCount = 0
  IsoHidden = false
  IsoVisible = false
  LockPosition = false
  NameGeomPattern = Diamond
  Perspective = false
  Rotation = -90
  Scale = 0.2
  ScaleType = 2
  ScrubCount = 1
  SeamHidden = false
  SeamVisible = true
  SectionDirection = 4
  SectionLineStretch = 1
  SectionNormal = (-1,0,-1e-16)
  SectionOrigin = (-232,-391.5,182.5)
  SmoothHidden = false
  SmoothVisible = true
  Source = -> [Assembly]
  TrimAfterCut = false
  UsePreviousCut = false
  X = -40.3115
  XDirection = (1e-16,0,-1)
  Y = -19.2541
FEATURE [TechDraw::DrawViewDimension] Dimension005
  AngleOverride = false
  Arbitrary = false
  ArbitraryTolerances = false
  BoxCorners = (2) [(-88.3,-39.3,-1e-07),(88.3,39.3,1e-07)]
  EqualTolerance = true
  ExtensionAngle = 0
  FormatSpec = %.2w
  FormatSpecOverTolerance = %+.2w
  FormatSpecUnderTolerance = %+.2w
  Inverted = false
  LineAngle = 0
  LockPosition = false
  MeasureType = 1
  OverTolerance = 0
  References2D = -> [SectionView]
  Rotation = 0
  ScaleType = 0
  TheoreticalExact = false
  Type = 0
  UnderTolerance = 0
  X = -73.966
  Y = -2.3022
FEATURE [TechDraw::DrawViewDimension] Dimension006
  AngleOverride = false
  Arbitrary = false
  ArbitraryTolerances = false
  BoxCorners = (2) [(-88.3,-39.3,-1e-07),(88.3,39.3,1e-07)]
  EqualTolerance = true
  ExtensionAngle = 0
  FormatSpec = %.2w
  FormatSpecOverTolerance = %+.2w
  FormatSpecUnderTolerance = %+.2w
  Inverted = false
  LineAngle = 0
  LockPosition = false
  MeasureType = 1
  OverTolerance = 0
  References2D = -> [SectionView]
  Rotation = 0
  ScaleType = 0
  TheoreticalExact = false
  Type = 0
  UnderTolerance = 0
  X = -42.5
  Y = -27.7983
FEATURE [TechDraw::DrawViewDimension] Dimension007
  AngleOverride = false
  Arbitrary = false
  ArbitraryTolerances = false
  BoxCorners = (2) [(-88.3,-39.3,-1e-07),(88.3,39.3,1e-07)]
  EqualTolerance = true
  ExtensionAngle = 0
  FormatSpec = %.2w
  FormatSpecOverTolerance = %+.2w
  FormatSpecUnderTolerance = %+.2w
  Inverted = false
  LineAngle = 0
  LockPosition = false
  MeasureType = 1
  OverTolerance = 0
  References2D = -> [SectionView]
  Rotation = 0
  ScaleType = 0
  TheoreticalExact = false
  Type = 0
  UnderTolerance = 0
  X = -23.3
  Y = -25.8642
FEATURE [TechDraw::DrawViewDimension] Dimension008
  AngleOverride = false
  Arbitrary = false
  ArbitraryTolerances = false
  BoxCorners = (2) [(-88.3,-39.3,-1e-07),(88.3,39.3,1e-07)]
  EqualTolerance = true
  ExtensionAngle = 0
  FormatSpec = %.2w
  FormatSpecOverTolerance = %+.2w
  FormatSpecUnderTolerance = %+.2w
  Inverted = false
  LineAngle = 0
  LockPosition = false
  MeasureType = 1
  OverTolerance = 0
  References2D = -> [SectionView]
  Rotation = 0
  ScaleType = 0
  TheoreticalExact = false
  Type = 0
  UnderTolerance = 0
  X = -4.1
  Y = -24.3061
FEATURE [TechDraw::DrawViewDimension] Dimension
  AngleOverride = false
  Arbitrary = false
  ArbitraryTolerances = false
  BoxCorners = (2) [(-52.5,-90.1,-1e-07),(52.5,90.1,1e-07)]
  EqualTolerance = true
  ExtensionAngle = 0
  FormatSpec = %.2w
  FormatSpecOverTolerance = %+.2w
  FormatSpecUnderTolerance = %+.2w
  Inverted = false
  LineAngle = 0
  LockPosition = false
  MeasureType = 1
  OverTolerance = 0
  References2D = -> [ProjItem002]
  Rotation = 0
  ScaleType = 0
  TheoreticalExact = false
  Type = 0
  UnderTolerance = 0
  X = 69.0011
  Y = 44.3402
FEATURE [TechDraw::DrawViewDimension] Dimension009
  AngleOverride = false
  Arbitrary = false
  ArbitraryTolerances = false
  BoxCorners = (2) [(-52.5,-90.1,-1e-07),(52.5,90.1,1e-07)]
  EqualTolerance = true
  ExtensionAngle = 0
  FormatSpec = %.2w
  FormatSpecOverTolerance = %+.2w
  FormatSpecUnderTolerance = %+.2w
  Inverted = false
  LineAngle = 0
  LockPosition = false
  MeasureType = 1
  OverTolerance = 0
  References2D = -> [ProjItem002]
  Rotation = 0
  ScaleType = 0
  TheoreticalExact = false
  Type = 0
  UnderTolerance = 0
  X = 69.0011
  Y = -13.0262
FEATURE [TechDraw::DrawViewDimension] Dimension010
  AngleOverride = false
  Arbitrary = false
  ArbitraryTolerances = false
  BoxCorners = (2) [(-90.1,-39.3,0),(90.1,39.3,0)]
  EqualTolerance = true
  ExtensionAngle = 0
  FormatSpec = %.2w
  FormatSpecOverTolerance = %+.2w
  FormatSpecUnderTolerance = %+.2w
  Inverted = false
  LineAngle = 0
  LockPosition = false
  MeasureType = 1
  OverTolerance = 0
  References2D = -> [ProjItem001]
  Rotation = 0
  ScaleType = 0
  TheoreticalExact = false
  Type = 0
  UnderTolerance = 0
  X = 99.0103
  Y = -45.8591
FEATURE [TechDraw::DrawViewDimension] Dimension011
  AngleOverride = false
  Arbitrary = false
  ArbitraryTolerances = false
  BoxCorners = (2) [(-90.1,-39.3,0),(90.1,39.3,0)]
  EqualTolerance = true
  ExtensionAngle = 0
  FormatSpec = %.2w
  FormatSpecOverTolerance = %+.2w
  FormatSpecUnderTolerance = %+.2w
  Inverted = false
  LineAngle = 0
  LockPosition = false
  MeasureType = 1
  OverTolerance = 0
  References2D = -> [ProjItem001]
  Rotation = 0
  ScaleType = 0
  TheoreticalExact = false
  Type = 1
  UnderTolerance = 0
  X = -14.2408
  Y = 49.5379
FEATURE [TechDraw::DrawViewDimension] Dimension012
  AngleOverride = false
  Arbitrary = false
  ArbitraryTolerances = false
  BoxCorners = (2) [(-90.1,-39.3,0),(90.1,39.3,0)]
  EqualTolerance = true
  ExtensionAngle = 0
  FormatSpec = %.2w
  FormatSpecOverTolerance = %+.2w
  FormatSpecUnderTolerance = %+.2w
  Inverted = false
  LineAngle = 0
  LockPosition = false
  MeasureType = 1
  OverTolerance = 0
  References2D = -> [ProjItem001]
  Rotation = 0
  ScaleType = 0
  TheoreticalExact = false
  Type = 0
  UnderTolerance = 0
  X = 30.9807
  Y = -45.5454
FEATURE [TechDraw::DrawViewDimension] Dimension013
  AngleOverride = false
  Arbitrary = false
  ArbitraryTolerances = false
  BoxCorners = (2) [(-90.1,-39.3,0),(90.1,39.3,0)]
  EqualTolerance = true
  ExtensionAngle = 0
  FormatSpec = %.2w
  FormatSpecOverTolerance = %+.2w
  FormatSpecUnderTolerance = %+.2w
  Inverted = false
  LineAngle = 0
  LockPosition = false
  MeasureType = 1
  OverTolerance = 0
  References2D = -> [ProjItem001]
  Rotation = 0
  ScaleType = 0
  TheoreticalExact = false
  Type = 1
  UnderTolerance = 0
  X = 69.5
  Y = -45.5454
FEATURE [TechDraw::DrawViewDimension] Dimension014
  AngleOverride = false
  Arbitrary = false
  ArbitraryTolerances = false
  BoxCorners = (2) [(-90.1,-39.3,0),(90.1,39.3,0)]
  EqualTolerance = true
  ExtensionAngle = 0
  FormatSpec = %.2w
  FormatSpecOverTolerance = %+.2w
  FormatSpecUnderTolerance = %+.2w
  Inverted = false
  LineAngle = 0
  LockPosition = false
  MeasureType = 1
  OverTolerance = 0
  References2D = -> [ProjItem001]
  Rotation = 0
  ScaleType = 0
  TheoreticalExact = false
  Type = 1
  UnderTolerance = 0
  X = 80.7
  Y = -45.5454
FEATURE [TechDraw::DrawViewDimension] Dimension015
  AngleOverride = false
  Arbitrary = false
  ArbitraryTolerances = false
  BoxCorners = (2) [(-90.1,-39.3,0),(90.1,39.3,0)]
  EqualTolerance = true
  ExtensionAngle = 0
  FormatSpec = %.2w
  FormatSpecOverTolerance = %+.2w
  FormatSpecUnderTolerance = %+.2w
  Inverted = false
  LineAngle = 0
  LockPosition = false
  MeasureType = 1
  OverTolerance = 0
  References2D = -> [ProjItem001]
  Rotation = 0
  ScaleType = 0
  TheoreticalExact = false
  Type = 1
  UnderTolerance = 0
  X = -88.3
  Y = -45.5454
FEATURE [TechDraw::DrawViewDimension] Dimension016
  AngleOverride = false
  Arbitrary = false
  ArbitraryTolerances = false
  BoxCorners = (2) [(-85.7,-39.3,0),(85.7,39.3,0)]
  EqualTolerance = true
  ExtensionAngle = 0
  FormatSpec = %.2w
  FormatSpecOverTolerance = %+.2w
  FormatSpecUnderTolerance = %+.2w
  Inverted = false
  LineAngle = 0
  LockPosition = false
  MeasureType = 1
  OverTolerance = 0
  References2D = -> [ProjItem001]
  Rotation = 0
  ScaleType = 0
  TheoreticalExact = false
  Type = 2
  UnderTolerance = 0
  X = 93.547
  Y = 10.1522
FEATURE [TechDraw::DrawViewDimension] Dimension017
  AngleOverride = false
  Arbitrary = false
  ArbitraryTolerances = false
  BoxCorners = (2) [(-85.7,-39.3,-1e-07),(85.7,39.3,1e-07)]
  EqualTolerance = true
  ExtensionAngle = 0
  FormatSpec = %.2w
  FormatSpecOverTolerance = %+.2w
  FormatSpecUnderTolerance = %+.2w
  Inverted = false
  LineAngle = 0
  LockPosition = false
  MeasureType = 1
  OverTolerance = 0
  References2D = -> [SectionView]
  Rotation = 0
  ScaleType = 0
  TheoreticalExact = false
  Type = 0
  UnderTolerance = 0
  X = -35.9078
  Y = -17.3274
FEATURE [TechDraw::DrawViewDimension] Dimension018
  AngleOverride = false
  Arbitrary = false
  ArbitraryTolerances = false
  BoxCorners = (2) [(-85.7,-39.3,-1e-07),(85.7,39.3,1e-07)]
  EqualTolerance = true
  ExtensionAngle = 0
  FormatSpec = %.2w
  FormatSpecOverTolerance = %+.2w
  FormatSpecUnderTolerance = %+.2w
  Inverted = false
  LineAngle = 0
  LockPosition = false
  MeasureType = 1
  OverTolerance = 0
  References2D = -> [SectionView]
  Rotation = 0
  ScaleType = 0
  TheoreticalExact = false
  Type = 0
  UnderTolerance = 0
  X = -51.4331
  Y = -10.3274
FEATURE [TechDraw::DrawPage] Page
  KeepUpdated = true
  NextBalloonIndex = 1
  ProjectionType = 0
  Template = -> Template
  Views = -> [ProjGroup,SectionView,Dimension005,Dimension006,Dimension007,Dimension008,Dimension,Dimension009,Dimension010,Dimension011,Dimension012,Dimension013,Dimension014,Dimension015,Dimension016,Dimension017,Dimension018]
note: 2 file-system paths scrubbed to <path> (originals preserved in the JSON sidecar)

RESOLVED EXTERNAL PARTS (link-assembly join: the EXTERNAL_REF files above that resolve inside this repo's crawl, each included once):
---- part 10_drawer_96mm_assembly.FCStd = doc fcstd_513d27c35c83 ----
FCSTD DOCUMENT  (FreeCAD 1.0R39109 (Git))
Label: 10_drawer_96mm_assembly
License: All rights reserved
LicenseURL: http://en.wikipedia.org/wiki/All_rights_reserved
objects: App::FeaturePython×17, App::Link×6, Assembly::JointGroup×1, Assembly::AssemblyObject×1
EXTERNAL_REF file=60_drawer_all_bottom.FCStd obj=Body
EXTERNAL_REF file=15_drawer_96mm_long.FCStd obj=Body
EXTERNAL_REF file=16_drawer_96mm_short.FCStd obj=Body
EXTERNAL_REF file=17_drawer_96mm_front.FCStd obj=Body

FEATURE [App::Link] Body
  LinkedObject = -> <external 60_drawer_all_bottom.FCStd>#Body
FEATURE [App::FeaturePython] GroundedJoint  # Assembly grounded joint (typed FeaturePython)
  ObjectToGround = -> Body
FEATURE [App::Link] Body001
  LinkPlacement = pos=(-0.0692255,177.5,34.4999) rot=(0.999999,-0.001116,0.001116;1.5708rad)
  LinkedObject = -> <external 15_drawer_96mm_long.FCStd>#Body
  Placement = pos=(-0.0692255,177.5,34.4999) rot=(0.999999,-0.001116,0.001116;1.5708rad)
FEATURE [App::Link] Body002
  LinkPlacement = pos=(2.3e-15,-177.5,34) rot=(0,0.707107,0.707107;3.14159rad)
  LinkedObject = -> <external 15_drawer_96mm_long.FCStd>#Body
  Placement = pos=(2.3e-15,-177.5,34) rot=(0,0.707107,0.707107;3.14159rad)
FEATURE [App::Link] Body003
  LinkPlacement = pos=(-231.5,-4.06e-14,34) rot=(0.57735,0.57735,0.57735;2.0944rad)
  LinkedObject = -> <external 16_drawer_96mm_short.FCStd>#Body
  Placement = pos=(-231.5,-4.06e-14,34) rot=(0.57735,0.57735,0.57735;2.0944rad)
FEATURE [App::Link] Body004
  LinkPlacement = pos=(231.5,-6.4e-15,34) rot=(0.57735,-0.57735,-0.57735;2.0944rad)
  LinkedObject = -> <external 16_drawer_96mm_short.FCStd>#Body
  Placement = pos=(231.5,-6.4e-15,34) rot=(0.57735,-0.57735,-0.57735;2.0944rad)
FEATURE [App::FeaturePython] Joint  label="Back1"  # Assembly joint (typed FeaturePython)
  Activated = true
  AngleMax = 0
  AngleMin = 0
  Detach1 = false
  Detach2 = false
  Distance = 0
  Distance2 = 0
  EnableAngleMax = false
  EnableAngleMin = false
  EnableLengthMax = false
  EnableLengthMin = false
  JointType = 5 (Distance)
  LengthMax = 0
  LengthMin = 0
  Placement1 = pos=(-2.3e-15,168.5,3.25) rot=(-1,0,0;1.5708rad)
  Placement2 = pos=(6.54e-14,-30.75,9) rot=(0.707107,0.707107,0;3.14159rad)
  Reference1 = -> Assembly [Body.Face1,Body.Face1]
  Reference2 = -> Assembly [Body001.Face7,Body001.Face7]
FEATURE [App::FeaturePython] Joint001  label="Back2"  # Assembly joint (typed FeaturePython)
  Activated = true
  AngleMax = 0
  AngleMin = 0
  Detach1 = false
  Detach2 = false
  Distance = 0.5
  Distance2 = 0
  EnableAngleMax = false
  EnableAngleMin = false
  EnableLengthMax = false
  EnableLengthMin = false
  JointType = 5 (Distance)
  LengthMax = 0
  LengthMin = 0
  Placement1 = pos=(7.41e-14,-34,12) rot=(0.57735,0.57735,-0.57735;2.0944rad)
  Placement2 = pos=(-2e-16,4.1e-15,0) rot=(0,0,1;0rad)
  Reference1 = -> Assembly [Body001.Face8,Body001.Vertex9]
  Reference2 = -> Assembly [Body.Face5,Body.Vertex1]
FEATURE [App::FeaturePython] Joint002  label="Back3"  # Assembly joint (typed FeaturePython)
  Activated = true
  AngleMax = 0
  AngleMin = 0
  Detach1 = false
  Detach2 = false
  Distance = 6
  Distance2 = 0
  EnableAngleMax = false
  EnableAngleMin = false
  EnableLengthMax = false
  EnableLengthMin = false
  JointType = 5 (Distance)
  LengthMax = 0
  LengthMin = 0
  Placement1 = pos=(-216.5,1.03295,7.34884) rot=(-0.57735,-0.57735,0.57735;2.0944rad)
  Placement2 = pos=(-222.5,-5.2e-15,3.25) rot=(-0.57735,-0.57735,0.57735;2.0944rad)
  Reference1 = -> Assembly [Body001.Face2,Body001.Face2]
  Reference2 = -> Assembly [Body.Face4,Body.Face4]
FEATURE [App::FeaturePython] Joint003  label="Left1"  # Assembly joint (typed FeaturePython)
  Activated = true
  AngleMax = 0
  AngleMin = 0
  Detach1 = false
  Detach2 = false
  Distance = 0
  Distance2 = 0
  EnableAngleMax = false
  EnableAngleMin = false
  EnableLengthMax = false
  EnableLengthMin = false
  JointType = 5 (Distance)
  LengthMax = 0
  LengthMin = 0
  Placement1 = pos=(-2e-16,4.1e-15,6.5) rot=(0,0,1;0rad)
  Placement2 = pos=(2.8e-15,-27.5,12) rot=(-0.57735,-0.57735,-0.57735;2.0944rad)
  Reference1 = -> Assembly [Body.Face6,Body.Face6]
  Reference2 = -> Assembly [Body003.Face6,Body003.Face6]
FEATURE [App::FeaturePython] Joint004  label="Left2"  # Assembly joint (typed FeaturePython)
  Activated = true
  AngleMax = 0
  AngleMin = 0
  Detach1 = false
  Detach2 = false
  Distance = 0
  Distance2 = 0
  EnableAngleMax = false
  EnableAngleMin = false
  EnableLengthMax = false
  EnableLengthMin = false
  JointType = 5 (Distance)
  LengthMax = 0
  LengthMin = 0
  Placement1 = pos=(9.3e-15,-30.75,9) rot=(-0.707107,-0.707107,0;3.14159rad)
  Placement2 = pos=(-222.5,-5.2e-15,3.25) rot=(-0.57735,-0.57735,0.57735;2.0944rad)
  Reference1 = -> Assembly [Body003.Face7,Body003.Face7]
  Reference2 = -> Assembly [Body.Face4,Body.Face4]
FEATURE [App::FeaturePython] Joint005  label="Left3"  # Assembly joint (typed FeaturePython)
  Activated = true
  AngleMax = 0
  AngleMin = 0
  Detach1 = false
  Detach2 = false
  Distance = 9
  Distance2 = 0
  EnableAngleMax = false
  EnableAngleMin = false
  EnableLengthMax = false
  EnableLengthMin = false
  JointType = 5 (Distance)
  LengthMax = 0
  LengthMin = 0
  Placement1 = pos=(2.3e-15,-168.5,3.25) rot=(0,-0.707107,0.707107;3.14159rad)
  Placement2 = pos=(-177.5,1.03295,7.34884) rot=(-0.57735,-0.57735,0.57735;2.0944rad)
  Reference1 = -> Assembly [Body.Face3,Body.Face3]
  Reference2 = -> Assembly [Body003.Face2,Body003.Face2]
FEATURE [App::FeaturePython] Joint006  label="Distance"  # Assembly joint (typed FeaturePython)
  Activated = true
  AngleMax = 0
  AngleMin = 0
  Detach1 = false
  Detach2 = false
  Distance = 0
  Distance2 = 0
  EnableAngleMax = false
  EnableAngleMin = false
  EnableLengthMax = false
  EnableLengthMin = false
  JointType = 5 (Distance)
  LengthMax = 0
  LengthMin = 0
  Placement1 = pos=(6.6e-14,-27.5,12) rot=(-0.57735,-0.57735,-0.57735;2.0944rad)
  Placement2 = pos=(-2e-16,4.1e-15,6.5) rot=(0,0,1;0rad)
  Reference1 = -> Assembly [Body002.Face6,Body002.Face6]
  Reference2 = -> Assembly [Body.Face6,Body.Face6]
FEATURE [App::FeaturePython] Joint007  label="Distance001"  # Assembly joint (typed FeaturePython)
  Activated = true
  AngleMax = 0
  AngleMin = 0
  Detach1 = false
  Detach2 = false
  Distance = 0
  Distance2 = 0
  EnableAngleMax = false
  EnableAngleMin = false
  EnableLengthMax = false
  EnableLengthMin = false
  JointType = 5 (Distance)
  LengthMax = 0
  LengthMin = 0
  Placement1 = pos=(2.3e-15,-168.5,3.25) rot=(0,-0.707107,0.707107;3.14159rad)
  Placement2 = pos=(6.88e-14,-30.75,9) rot=(0.707107,0.707107,0;3.14159rad)
  Reference1 = -> Assembly [Body.Face3,Body.Face3]
  Reference2 = -> Assembly [Body002.Face7,Body002.Vertex8]
FEATURE [App::FeaturePython] Joint008  label="Distance002"  # Assembly joint (typed FeaturePython)
  Activated = true
  AngleMax = 0
  AngleMin = 0
  Detach1 = false
  Detach2 = false
  Distance = -6
  Distance2 = 0
  EnableAngleMax = false
  EnableAngleMin = false
  EnableLengthMax = false
  EnableLengthMin = false
  JointType = 5 (Distance)
  LengthMax = 0
  LengthMin = 0
  Placement1 = pos=(222.5,5.2e-15,3.25) rot=(0.57735,-0.57735,0.57735;4.18879rad)
  Placement2 = pos=(-216.5,1.03295,7.34884) rot=(-0.57735,-0.57735,0.57735;2.0944rad)
  Reference1 = -> Assembly [Body.Face2,Body.Face2]
  Reference2 = -> Assembly [Body002.Face2,Body002.Face2]
FEATURE [App::FeaturePython] Joint009  label="Rigth1"  # Assembly joint (typed FeaturePython)
  Activated = true
  AngleMax = 0
  AngleMin = 0
  Detach1 = false
  Detach2 = false
  Distance = 0
  Distance2 = 0
  EnableAngleMax = false
  EnableAngleMin = false
  EnableLengthMax = false
  EnableLengthMin = false
  JointType = 5 (Distance)
  LengthMax = 0
  LengthMin = 0
  Placement1 = pos=(-1.05e-14,-27.5,12) rot=(0.57735,0.57735,0.57735;4.18879rad)
  Placement2 = pos=(-2e-16,4.1e-15,6.5) rot=(0,0,1;0rad)
  Reference1 = -> Assembly [Body004.Face6,Body004.Face6]
  Reference2 = -> Assembly [Body.Face6,Body.Face6]
FEATURE [App::FeaturePython] Joint010  label="Rigth2"  # Assembly joint (typed FeaturePython)
  Activated = true
  AngleMax = 0
  AngleMin = 0
  Detach1 = false
  Detach2 = false
  Distance = 0
  Distance2 = 0
  EnableAngleMax = false
  EnableAngleMin = false
  EnableLengthMax = false
  EnableLengthMin = false
  JointType = 5 (Distance)
  LengthMax = 0
  LengthMin = 0
  Placement1 = pos=(-4.9e-15,-30.75,9) rot=(0.707107,0.707107,0;3.14159rad)
  Placement2 = pos=(222.5,5.2e-15,3.25) rot=(0.57735,-0.57735,0.57735;4.18879rad)
  Reference1 = -> Assembly [Body004.Face7,Body004.Vertex8]
  Reference2 = -> Assembly [Body.Face2,Body.Vertex5]
FEATURE [App::FeaturePython] Joint011  label="Right3"  # Assembly joint (typed FeaturePython)
  Activated = true
  AngleMax = 0
  AngleMin = 0
  Detach1 = false
  Detach2 = false
  Distance = 9
  Distance2 = 0
  EnableAngleMax = false
  EnableAngleMin = false
  EnableLengthMax = false
  EnableLengthMin = false
  JointType = 5 (Distance)
  LengthMax = 0
  LengthMin = 0
  Placement1 = pos=(2.3e-15,-168.5,3.25) rot=(0,-0.707107,0.707107;3.14159rad)
  Placement2 = pos=(177.5,1.03295,7.34884) rot=(0.57735,-0.57735,0.57735;4.18879rad)
  Reference1 = -> Assembly [Body.Face3,Body.Vertex5]
  Reference2 = -> Assembly [Body004.Face3,Body004.Face3]
FEATURE [App::Link] Body005
  LinkPlacement = pos=(2.5e-15,-177.5,33.5) rot=(0,-0.707107,0.707107;3.14159rad)
  LinkedObject = -> <external 17_drawer_96mm_front.FCStd>#Body
  Placement = pos=(2.5e-15,-177.5,33.5) rot=(0,-0.707107,0.707107;3.14159rad)
FEATURE [App::FeaturePython] Joint012  label="Front1"  # Assembly joint (typed FeaturePython)
  Activated = true
  AngleMax = 0
  AngleMin = 0
  Detach1 = false
  Detach2 = false
  Distance = 0
  Distance2 = 0
  EnableAngleMax = false
  EnableAngleMin = false
  EnableLengthMax = false
  EnableLengthMin = false
  JointType = 5 (Distance)
  LengthMax = 0
  LengthMin = 0
  Placement1 = pos=(2e-15,0,0) rot=(0,0,1;0rad)
  Placement2 = pos=(3e-15,0,0) rot=(0,0,1;0rad)
  Reference1 = -> Assembly [Body005.Face5,Body005.Face5]
  Reference2 = -> Assembly [Body002.Face4,Body002.Face4]
FEATURE [App::FeaturePython] Joint013  label="Front2"  # Assembly joint (typed FeaturePython)
  Activated = true
  AngleMax = 0
  AngleMin = 0
  Detach1 = false
  Detach2 = false
  Distance = 6
  Distance2 = 0
  EnableAngleMax = false
  EnableAngleMin = false
  EnableLengthMax = false
  EnableLengthMin = false
  JointType = 5 (Distance)
  LengthMax = 0
  LengthMin = 0
  Placement1 = pos=(8.3e-15,40,7.5) rot=(-1,0,0;1.5708rad)
  Placement2 = pos=(7.1e-15,-46.5,7.5) rot=(0,0.707107,-0.707107;3.14159rad)
  Reference1 = -> Assembly [Body002.Face1,Body002.Face1]
  Reference2 = -> Assembly [Body005.Face3,Body005.Face3]
FEATURE [App::FeaturePython] Joint014  label="Distance003"  # Assembly joint (typed FeaturePython)
  Activated = true
  AngleMax = 0
  AngleMin = 0
  Detach1 = false
  Detach2 = false
  Distance = -29
  Distance2 = 0
  EnableAngleMax = false
  EnableAngleMin = false
  EnableLengthMax = false
  EnableLengthMin = false
  JointType = 5 (Distance)
  LengthMax = 0
  LengthMin = 0
  Placement1 = pos=(1.4e-15,0,0) rot=(0,0,1;0rad)
  Placement2 = pos=(260.5,0,7.5) rot=(-0.57735,0.57735,-0.57735;2.0944rad)
  Reference1 = -> Assembly [Body003.Face4,Body003.Face4]
  Reference2 = -> Assembly [Body005.Face2,Body005.Face2]
FEATURE [App::FeaturePython] Joint015  label="Distance004"  # Assembly joint (typed FeaturePython)
  Activated = true
  AngleMax = 0
  AngleMin = 0
  Detach1 = false
  Detach2 = false
  Distance = 0
  Distance2 = 0
  EnableAngleMax = false
  EnableAngleMin = false
  EnableLengthMax = false
  EnableLengthMin = false
  JointType = 5 (Distance)
  LengthMax = 0
  LengthMin = 0
  Placement1 = pos=(1.72e-14,40,7.5) rot=(-1,0,0;1.5708rad)
  Placement2 = pos=(6.2e-15,40,7.5) rot=(-1,0,0;1.5708rad)
  Reference1 = -> Assembly [Body001.Face1,Body001.Vertex2]
  Reference2 = -> Assembly [Body003.Face1,Body003.Vertex4]
FEATURE [Assembly::JointGroup] Joints
  Group = -> [GroundedJoint,Joint,Joint001,Joint002,Joint003,Joint004,Joint005,Joint006,Joint007,Joint008,Joint009,Joint010,Joint011,Joint012,Joint013,Joint014,Joint015]
FEATURE [Assembly::AssemblyObject] Assembly
  Group = -> [Joints,Body,GroundedJoint,Body001,Body002,Body003,Body004,Joint,Joint001,Joint002,Joint003,Joint004,Joint005,Joint006,Joint007,Joint008,Joint009,Joint010,Joint011,Body005,Joint012,Joint013,Joint014,Joint015]
  Origin = -> Origin
  Type = Assembly
---- part 70_drawer_box_assembly.FCStd = doc fcstd_3038d1ece339 ----
FCSTD DOCUMENT  (FreeCAD 1.0R39109 (Git))
Label: 70_drawer_box_assembly
License: All rights reserved
LicenseURL: http://en.wikipedia.org/wiki/All_rights_reserved
objects: App::FeaturePython×25, App::Link×9, TechDraw::DrawViewDimension×7, TechDraw::DrawProjGroupItem×5, Assembly::JointGroup×2, Assembly::AssemblyObject×2, TechDraw::DrawSVGTemplate×1, TechDraw::DrawProjGroup×1, TechDraw::DrawPage×1
note: 13 computed .brp shape members not serialized (recipe doc carries the construction recipe); baked Part::Feature solids carry a one-line shape summary decoded from their .brp
EXTERNAL_REF file=71_drawer_box_top_bottom.FCStd obj=Body
EXTERNAL_REF file=73_drawer_box_side_b.FCStd obj=Body
EXTERNAL_REF file=72_drawer_box_side_a.FCStd obj=Body
EXTERNAL_REF file=junker_kv1-45-h45-l300-sc/kv1_h45_l350.FCStd obj=KV1_45_H45_L____SC
EXTERNAL_REF file=75_drawer_box_stabilizer.FCStd obj=Body

FEATURE [App::Link] Body
  LinkPlacement = pos=(0,0,0) rot=(0,0,1;3.14159rad)
  LinkedObject = -> <external 71_drawer_box_top_bottom.FCStd>#Body
  Placement = pos=(0,0,0) rot=(0,0,1;3.14159rad)
FEATURE [App::FeaturePython] GroundedJoint  # Assembly grounded joint (typed FeaturePython)
  ObjectToGround = -> Body
  Placement = pos=(0,0,0) rot=(0,0,1;3.14159rad)
FEATURE [App::Link] Body003
  LinkPlacement = pos=(2.045e-13,-6.16e-14,-771) rot=(1,0,0;3.14159rad)
  LinkedObject = -> <external 71_drawer_box_top_bottom.FCStd>#Body
  Placement = pos=(2.045e-13,-6.16e-14,-771) rot=(1,0,0;3.14159rad)
FEATURE [App::Link] Body004
  LinkPlacement = pos=(-262.5,7.5,-385.5) rot=(0,1,0;1.5708rad)
  LinkedObject = -> <external 73_drawer_box_side_b.FCStd>#Body
  Placement = pos=(-262.5,7.5,-385.5) rot=(0,1,0;1.5708rad)
FEATURE [App::Link] Body005
  LinkPlacement = pos=(244.5,7.5,-385.5) rot=(0,1,0;1.5708rad)
  LinkedObject = -> <external 72_drawer_box_side_a.FCStd>#Body
  Placement = pos=(244.5,7.5,-385.5) rot=(0,1,0;1.5708rad)
FEATURE [App::Link] KV1_45_H45_L____SC  label="KV1-45-H45-L...-SC"
  LinkPlacement = pos=(238.45,-31,-32) rot=(0,0.707107,-0.707107;3.14159rad)
  LinkedObject = -> <external junker_kv1-45-h45-l300-sc/kv1_h45_l350.FCStd>#KV1_45_H45_L____SC
  Placement = pos=(238.45,-31,-32) rot=(0,0.707107,-0.707107;3.14159rad)
FEATURE [TechDraw::DrawSVGTemplate] Template
  Height = 210
  Orientation = 1
  Template = C:/Program Files/FreeCAD 1.0/data/Mod/TechDraw/Templates/Default_Template_A4_Landscape.svg
  Width = 297
FEATURE [TechDraw::DrawProjGroupItem] View  label="Front"
  CoarseView = false
  Direction = (0,-1,0)
  Focus = 100
  HardHidden = false
  IsoCount = 0
  IsoHidden = false
  IsoVisible = false
  LockPosition = true
  Perspective = false
  Rotation = 0
  RotationVector = (1,0,0)
  Scale = 0.1
  ScaleType = 2
  ScrubCount = 1
  SeamHidden = false
  SeamVisible = true
  SmoothHidden = false
  SmoothVisible = true
  Type = 0
  X = 0
  XDirection = (1,0,0)
  XSource = -> [Body,Body003,Body004,Body005,KV1_45_H45_L____SC,Body007]
  Y = 0
FEATURE [TechDraw::DrawProjGroupItem] ProjItem  label="Right"
  CoarseView = false
  Direction = (1,-1e-16,0)
  Focus = 100
  HardHidden = false
  IsoCount = 0
  IsoHidden = false
  IsoVisible = false
  LockPosition = false
  Perspective = false
  Rotation = 0
  RotationVector = (1,0,0)
  ScaleType = 0
  ScrubCount = 1
  SeamHidden = false
  SeamVisible = true
  SmoothHidden = false
  SmoothVisible = true
  Type = 2
  X = -60.9
  XDirection = (1e-16,1,0)
  XSource = -> [Body,Body003,Body004,Body005,KV1_45_H45_L____SC,Body007]
  Y = 0
FEATURE [TechDraw::DrawProjGroupItem] ProjItem001  label="Bottom"
  CoarseView = false
  Direction = (0,0,-1)
  Focus = 100
  HardHidden = false
  IsoCount = 0
  IsoHidden = false
  IsoVisible = false
  LockPosition = false
  Perspective = false
  Rotation = 0
  RotationVector = (1,0,0)
  ScaleType = 0
  ScrubCount = 1
  SeamHidden = false
  SeamVisible = true
  SmoothHidden = false
  SmoothVisible = true
  Type = 5
  X = 0
  XDirection = (1,0,0)
  XSource = -> [Body,Body003,Body004,Body005,KV1_45_H45_L____SC,Body007]
  Y = 75
FEATURE [TechDraw::DrawProjGroupItem] ProjItem002  label="Left"
  CoarseView = false
  Direction = (-1,-1e-16,0)
  Focus = 100
  HardHidden = false
  IsoCount = 0
  IsoHidden = false
  IsoVisible = false
  LockPosition = false
  Perspective = false
  Rotation = 0
  RotationVector = (1,0,0)
  ScaleType = 0
  ScrubCount = 1
  SeamHidden = false
  SeamVisible = true
  SmoothHidden = false
  SmoothVisible = true
  Type = 1
  X = 60.9
  XDirection = (1e-16,-1,0)
  XSource = -> [Body,Body003,Body004,Body005,KV1_45_H45_L____SC,Body007]
  Y = 0
FEATURE [TechDraw::DrawProjGroupItem] ProjItem003  label="Top"
  CoarseView = false
  Direction = (0,0,1)
  Focus = 100
  HardHidden = false
  IsoCount = 0
  IsoHidden = false
  IsoVisible = false
  LockPosition = false
  Perspective = false
  Rotation = 0
  RotationVector = (1,0,0)
  ScaleType = 0
  ScrubCount = 1
  SeamHidden = false
  SeamVisible = true
  SmoothHidden = false
  SmoothVisible = true
  Type = 4
  X = 0
  XDirection = (1,0,0)
  XSource = -> [Body,Body003,Body004,Body005,KV1_45_H45_L____SC,Body007]
  Y = -75
FEATURE [TechDraw::DrawProjGroup] ProjGroup
  Anchor = -> View
  AutoDistribute = true
  LockPosition = false
  ProjectionType = 0
  Rotation = 0
  Scale = 0.1
  ScaleType = 2
  Views = -> [View,ProjItem,ProjItem001,ProjItem002,ProjItem003]
  X = 148.5
  XSource = -> [Body,Body003,Body004,Body005,KV1_45_H45_L____SC,Body007]
  Y = 105
  spacingX = 15
  spacingY = 15
FEATURE [TechDraw::DrawViewDimension] Dimension
  AngleOverride = false
  Arbitrary = false
  ArbitraryTolerances = false
  BoxCorners = (2) [(-26.25,-40.35,0),(26.25,40.35,0)]
  EqualTolerance = true
  ExtensionAngle = 0
  FormatSpec = %.2w
  FormatSpecOverTolerance = %+.2w
  FormatSpecUnderTolerance = %+.2w
  Inverted = false
  LineAngle = 0
  LockPosition = false
  MeasureType = 1
  OverTolerance = 0
  References2D = -> [View]
  Rotation = 0
  ScaleType = 0
  TheoreticalExact = false
  Type = 0
  UnderTolerance = 0
  X = 32.776
  Y = -39.775
FEATURE [TechDraw::DrawViewDimension] Dimension001
  AngleOverride = false
  Arbitrary = false
  ArbitraryTolerances = false
  BoxCorners = (2) [(-26.25,-40.35,0),(26.25,40.35,0)]
  EqualTolerance = true
  ExtensionAngle = 0
  FormatSpec = %.2w
  FormatSpecOverTolerance = %+.2w
  FormatSpecUnderTolerance = %+.2w
  Inverted = false
  LineAngle = 0
  LockPosition = false
  MeasureType = 1
  OverTolerance = 0
  References2D = -> [View]
  Rotation = 0
  ScaleType = 0
  TheoreticalExact = false
  Type = 0
  UnderTolerance = 0
  X = 32.776
  Y = 35.9189
FEATURE [TechDraw::DrawViewDimension] Dimension002
  AngleOverride = false
  Arbitrary = false
  ArbitraryTolerances = false
  BoxCorners = (2) [(-26.25,-40.35,0),(26.25,40.35,0)]
  EqualTolerance = true
  ExtensionAngle = 0
  FormatSpec = %.2w
  FormatSpecOverTolerance = %+.2w
  FormatSpecUnderTolerance = %+.2w
  Inverted = false
  LineAngle = 0
  LockPosition = false
  MeasureType = 1
  OverTolerance = 0
  References2D = -> [View]
  Rotation = 0
  ScaleType = 0
  TheoreticalExact = false
  Type = 0
  UnderTolerance = 0
  X = 36.8541
  Y = 21.3236
FEATURE [App::Link] Body007
  LinkPlacement = pos=(-2.61e-14,196.5,-386) rot=(0,-0.707107,0.707107;3.14159rad)
  LinkedObject = -> <external 75_drawer_box_stabilizer.FCStd>#Body
  Placement = pos=(-2.61e-14,196.5,-386) rot=(0,-0.707107,0.707107;3.14159rad)
FEATURE [App::FeaturePython] Joint  label="Distance"  # Assembly joint (typed FeaturePython)
  Activated = true
  AngleMax = 0
  AngleMin = 0
  Detach1 = false
  Detach2 = false
  Distance = 0
  Distance2 = 0
  EnableAngleMax = false
  EnableAngleMin = false
  EnableLengthMax = false
  EnableLengthMin = false
  JointType = 5 (Distance)
  LengthMax = 0
  LengthMin = 0
  Placement1 = pos=(-385.5,-1.21012,9.03703) rot=(-0.57735,-0.57735,0.57735;2.0944rad)
  Placement2 = pos=(5.5e-15,3.01501,0) rot=(0,0,1;0rad)
  Reference1 = -> Assembly [Body005.Face2,Body005.Vertex7]
  Reference2 = -> Assembly [Body.Face4,Body.Vertex10]
FEATURE [App::FeaturePython] Joint001  label="Distance001"  # Assembly joint (typed FeaturePython)
  Activated = true
  AngleMax = 0
  AngleMin = 0
  Detach1 = false
  Detach2 = false
  Distance = 0
  Distance2 = 0
  EnableAngleMax = false
  EnableAngleMin = false
  EnableLengthMax = false
  EnableLengthMin = false
  JointType = 5 (Distance)
  LengthMax = 0
  LengthMin = 0
  Placement1 = pos=(0,189,9) rot=(-1,0,0;1.5708rad)
  Placement2 = pos=(-5.9e-15,-196.5,9) rot=(0,0.707107,-0.707107;3.14159rad)
  Reference1 = -> Assembly [Body005.Face1,Body005.Vertex2]
  Reference2 = -> Assembly [Body.Face6,Body.Vertex6]
FEATURE [App::FeaturePython] Joint002  label="Distance002"  # Assembly joint (typed FeaturePython)
  Activated = true
  AngleMax = 0
  AngleMin = 0
  Detach1 = false
  Detach2 = false
  Distance = 0
  Distance2 = 0
  EnableAngleMax = false
  EnableAngleMin = false
  EnableLengthMax = false
  EnableLengthMin = false
  JointType = 5 (Distance)
  LengthMax = 0
  LengthMin = 0
  Placement1 = pos=(-262.5,-4.6e-15,9) rot=(-0.57735,-0.57735,0.57735;2.0944rad)
  Placement2 = pos=(0,3.6e-15,18) rot=(0,0,1;0rad)
  Reference1 = -> Assembly [Body.Face2,Body.Vertex6]
  Reference2 = -> Assembly [Body005.Face5,Body005.Vertex2]
FEATURE [App::FeaturePython] Joint003  label="Distance003"  # Assembly joint (typed FeaturePython)
  Activated = true
  AngleMax = 0
  AngleMin = 0
  Detach1 = false
  Detach2 = false
  Distance = 0
  Distance2 = 0
  EnableAngleMax = false
  EnableAngleMin = false
  EnableLengthMax = false
  EnableLengthMin = false
  JointType = 5 (Distance)
  LengthMax = 0
  LengthMin = 0
  Placement1 = pos=(-385.5,-1.21012,8.96297) rot=(-0.57735,-0.57735,0.57735;2.0944rad)
  Placement2 = pos=(5.5e-15,3.01501,0) rot=(0,0,1;0rad)
  Reference1 = -> Assembly [Body004.Face2,Body004.Face2]
  Reference2 = -> Assembly [Body.Face4,Body.Vertex3]
FEATURE [App::FeaturePython] Joint004  label="Distance004"  # Assembly joint (typed FeaturePython)
  Activated = true
  AngleMax = 0
  AngleMin = 0
  Detach1 = false
  Detach2 = false
  Distance = 0
  Distance2 = 0
  EnableAngleMax = false
  EnableAngleMin = false
  EnableLengthMax = false
  EnableLengthMin = false
  JointType = 5 (Distance)
  LengthMax = 0
  LengthMin = 0
  Placement1 = pos=(-5.9e-15,-196.5,9) rot=(0,0.707107,-0.707107;3.14159rad)
  Placement2 = pos=(0,189,9) rot=(-1,0,0;1.5708rad)
  Reference1 = -> Assembly [Body.Face6,Body.Vertex7]
  Reference2 = -> Assembly [Body004.Face1,Body004.Vertex1]
FEATURE [App::FeaturePython] Joint005  label="Distance005"  # Assembly joint (typed FeaturePython)
  Activated = true
  AngleMax = 0
  AngleMin = 0
  Detach1 = false
  Detach2 = false
  Distance = 0
  Distance2 = 0
  EnableAngleMax = false
  EnableAngleMin = false
  EnableLengthMax = false
  EnableLengthMin = false
  JointType = 5 (Distance)
  LengthMax = 0
  LengthMin = 0
  Placement1 = pos=(262.5,4.6e-15,9) rot=(-0.57735,0.57735,-0.57735;2.0944rad)
  Placement2 = pos=(0,7.1e-15,0) rot=(0,0,1;0rad)
  Reference1 = -> Assembly [Body.Face3,Body.Vertex8]
  Reference2 = -> Assembly [Body004.Face4,Body004.Vertex1]
FEATURE [App::FeaturePython] Joint006  label="Distance006"  # Assembly joint (typed FeaturePython)
  Activated = true
  AngleMax = 0
  AngleMin = 0
  Detach1 = false
  Detach2 = false
  Distance = 0
  Distance2 = 0
  EnableAngleMax = false
  EnableAngleMin = false
  EnableLengthMax = false
  EnableLengthMin = false
  JointType = 5 (Distance)
  LengthMax = 0
  LengthMin = 0
  Placement1 = pos=(-262.5,-6.4e-15,9) rot=(-0.57735,-0.57735,0.57735;2.0944rad)
  Placement2 = pos=(0,7.1e-15,0) rot=(0,0,1;0rad)
  Reference1 = -> Assembly [Body003.Face2,Body003.Vertex1]
  Reference2 = -> Assembly [Body004.Face4,Body004.Vertex3]
FEATURE [App::FeaturePython] Joint007  label="Distance007"  # Assembly joint (typed FeaturePython)
  Activated = true
  AngleMax = 0
  AngleMin = 0
  Detach1 = false
  Detach2 = false
  Distance = 0
  Distance2 = 0
  EnableAngleMax = false
  EnableAngleMin = false
  EnableLengthMax = false
  EnableLengthMin = false
  JointType = 5 (Distance)
  LengthMax = 0
  LengthMin = 0
  Placement1 = pos=(4.7e-15,3.01501,0) rot=(0,0,1;0rad)
  Placement2 = pos=(385.5,-1.21012,8.96297) rot=(-0.57735,0.57735,-0.57735;2.0944rad)
  Reference1 = -> Assembly [Body003.Face4,Body003.Vertex1]
  Reference2 = -> Assembly [Body004.Face3,Body004.Vertex13]
FEATURE [App::FeaturePython] Joint008  label="Distance008"  # Assembly joint (typed FeaturePython)
  Activated = true
  AngleMax = 0
  AngleMin = 0
  Detach1 = false
  Detach2 = false
  Distance = 0
  Distance2 = 0
  EnableAngleMax = false
  EnableAngleMin = false
  EnableLengthMax = false
  EnableLengthMin = false
  JointType = 5 (Distance)
  LengthMax = 0
  LengthMin = 0
  Placement1 = pos=(-2e-16,-196.5,9) rot=(0,0.707107,-0.707107;3.14159rad)
  Placement2 = pos=(0,189,9) rot=(-1,0,0;1.5708rad)
  Reference1 = -> Assembly [Body003.Face6,Body003.Vertex5]
  Reference2 = -> Assembly [Body004.Face1,Body004.Vertex4]
FEATURE [App::FeaturePython] Joint009  label="Distance009"  # Assembly joint (typed FeaturePython)
  Activated = true
  AngleMax = 0
  AngleMin = 0
  Detach1 = false
  Detach2 = false
  Distance = 0
  Distance2 = 0
  EnableAngleMax = false
  EnableAngleMin = false
  EnableLengthMax = false
  EnableLengthMin = false
  JointType = 5 (Distance)
  LengthMax = 0
  LengthMin = 0
  Placement1 = pos=(-244.5,7.39e-13,8.98683) rot=(0.57735,0.57735,-0.57735;4.18879rad)
  Placement2 = pos=(0.0538161,-6.11853,0) rot=(0,0,1;0rad)
  Reference1 = -> Assembly [Body007.Face5,Body007.Face5]
  Reference2 = -> Assembly [Body005.Face6,Body005.Vertex47]
FEATURE [App::FeaturePython] Joint010  label="Distance010"  # Assembly joint (typed FeaturePython)
  Activated = true
  AngleMax = 0
  AngleMin = 0
  Detach1 = false
  Detach2 = false
  Distance = 0
  Distance2 = 0
  EnableAngleMax = false
  EnableAngleMin = false
  EnableLengthMax = false
  EnableLengthMin = false
  JointType = 5 (Distance)
  LengthMax = 0
  LengthMin = 0
  Placement1 = pos=(-1.29e-14,0,0) rot=(0,0,1;0rad)
  Placement2 = pos=(0,189,9) rot=(-1,0,0;1.5708rad)
  Reference1 = -> Assembly [Body007.Face2,Body007.Face2]
  Reference2 = -> Assembly [Body004.Face1,Body004.Face1]
FEATURE [App::FeaturePython] Joint011  label="Distance011"  # Assembly joint (typed FeaturePython)
  Activated = true
  AngleMax = 0
  AngleMin = 0
  Detach1 = false
  Detach2 = false
  Distance = 335.5
  Distance2 = 0
  EnableAngleMax = false
  EnableAngleMin = false
  EnableLengthMax = false
  EnableLengthMin = false
  JointType = 5 (Distance)
  LengthMax = 0
  LengthMin = 0
  Placement1 = pos=(-8.8e-15,-50.5,3) rot=(0,0.707107,-0.707107;3.14159rad)
  Placement2 = pos=(5.5e-15,3.01501,0) rot=(0,0,1;0rad)
  Reference1 = -> Assembly [Body007.Face6,Body007.Face6]
  Reference2 = -> Assembly [Body.Face4,Body.Vertex10]
  expr: Distance = (771 - 100) / 2
FEATURE [App::FeaturePython] Joint012  label="Distance012"  # Assembly joint (typed FeaturePython)
  Activated = true
  AngleMax = 0
  AngleMin = 0
  Detach1 = false
  Detach2 = false
  Distance = 0
  Distance2 = 0
  EnableAngleMax = false
  EnableAngleMin = false
  EnableLengthMax = false
  EnableLengthMin = false
  JointType = 5 (Distance)
  LengthMax = 0
  LengthMin = 0
  Placement1 = pos=(-1.2,0.000268538,-180.383) rot=(-0.57735,-0.57735,0.57735;2.0944rad)
  Placement2 = pos=(0.0538161,-6.11853,0) rot=(0,0,1;0rad)
  Reference1 = -> Assembly [KV1_45_H45_L____SC.Junker_H45SC_op_350.Part__Feature.Face126,KV1_45_H45_L____SC.Junker_H45SC_op_350.Part__Feature.Vertex163]
  Reference2 = -> Assembly [Body005.Face6,Body005.Vertex6]
FEATURE [App::FeaturePython] Joint013  label="Distance013"  # Assembly joint (typed FeaturePython)
  Activated = true
  AngleMax = 0
  AngleMin = 0
  Detach1 = false
  Detach2 = false
  Distance = -0.5
  Distance2 = 0
  EnableAngleMax = false
  EnableAngleMin = false
  EnableLengthMax = false
  EnableLengthMin = false
  JointType = 5 (Distance)
  LengthMax = 0
  LengthMin = 0
  Placement1 = pos=(0,-189,9) rot=(0,-0.707107,0.707107;3.14159rad)
  Placement2 = pos=(1.78975,1.17e-14,0) rot=(0,0,1;0rad)
  Reference1 = -> Assembly [Body005.Face10,Body005.Face10]
  Reference2 = -> Assembly [KV1_45_H45_L____SC.Junker_H45SC_op_350.Part__Feature.Face145,KV1_45_H45_L____SC.Junker_H45SC_op_350.Part__Feature.Face145]
FEATURE [App::FeaturePython] Joint014  label="Cylindrical"  # Assembly joint (typed FeaturePython)
  Activated = true
  AngleMax = 0
  AngleMin = 0
  Detach1 = false
  Detach2 = false
  Distance = 0
  Distance2 = 0
  EnableAngleMax = false
  EnableAngleMin = false
  EnableLengthMax = false
  EnableLengthMin = false
  JointType = 2 (Cylindrical)
  LengthMax = 0
  LengthMin = 0
  Placement1 = pos=(-353.5,-81,4.5) rot=(0,0,1;0rad)
  Placement2 = pos=(-0.6,0,-107.5) rot=(0,1,0;1.5708rad)
  Reference1 = -> Assembly [Body005.Face11,Body005.Face11]
  Reference2 = -> Assembly [KV1_45_H45_L____SC.Junker_H45SC_op_350.Part__Feature.Face31,KV1_45_H45_L____SC.Junker_H45SC_op_350.Part__Feature.Face31]
FEATURE [Assembly::JointGroup] Joints001
FEATURE [Assembly::AssemblyObject] Assembly001
  Group = -> [Joints001]
  Origin = -> Origin001
  Type = Assembly
FEATURE [App::Link] KV1_45_H45_L____SC001  label="KV1-45-H45-L...-SC001"
  LinkPlacement = pos=(238.45,-31,-224) rot=(0,0.707107,-0.707107;3.14159rad)
  LinkedObject = -> <external junker_kv1-45-h45-l300-sc/kv1_h45_l350.FCStd>#KV1_45_H45_L____SC
  Placement = pos=(238.45,-31,-224) rot=(0,0.707107,-0.707107;3.14159rad)
FEATURE [App::Link] KV1_45_H45_L____SC002  label="KV1-45-H45-L...-SC002"
  LinkPlacement = pos=(238.45,-31,-128) rot=(0,0.707107,-0.707107;3.14159rad)
  LinkedObject = -> <external junker_kv1-45-h45-l300-sc/kv1_h45_l350.FCStd>#KV1_45_H45_L____SC
  Placement = pos=(238.45,-31,-128) rot=(0,0.707107,-0.707107;3.14159rad)
FEATURE [App::Link] KV1_45_H45_L____SC003  label="KV1-45-H45-L...-SC003"
  LinkPlacement = pos=(238.45,-31,-320) rot=(0,0.707107,-0.707107;3.14159rad)
  LinkedObject = -> <external junker_kv1-45-h45-l300-sc/kv1_h45_l350.FCStd>#KV1_45_H45_L____SC
  Placement = pos=(238.45,-31,-320) rot=(0,0.707107,-0.707107;3.14159rad)
FEATURE [App::FeaturePython] Joint015  label="Distance014"  # Assembly joint (typed FeaturePython)
  Activated = true
  AngleMax = 0
  AngleMin = 0
  Detach1 = false
  Detach2 = false
  Distance = 0
  Distance2 = 0
  EnableAngleMax = false
  EnableAngleMin = false
  EnableLengthMax = false
  EnableLengthMin = false
  JointType = 5 (Distance)
  LengthMax = 0
  LengthMin = 0
  Placement1 = pos=(-1.2,0.000268538,-180.383) rot=(-0.57735,-0.57735,0.57735;2.0944rad)
  Placement2 = pos=(0.0538161,-6.11853,0) rot=(0,0,1;0rad)
  Reference1 = -> Assembly [KV1_45_H45_L____SC002.Junker_H45SC_op_350.Part__Feature.Face126,KV1_45_H45_L____SC002.Junker_H45SC_op_350.Part__Feature.Vertex163]
  Reference2 = -> Assembly [Body005.Face6,Body005.Vertex23]
FEATURE [App::FeaturePython] Joint016  label="Distance015"  # Assembly joint (typed FeaturePython)
  Activated = true
  AngleMax = 0
  AngleMin = 0
  Detach1 = false
  Detach2 = false
  Distance = -0.5
  Distance2 = 0
  EnableAngleMax = false
  EnableAngleMin = false
  EnableLengthMax = false
  EnableLengthMin = false
  JointType = 5 (Distance)
  LengthMax = 0
  LengthMin = 0
  Placement1 = pos=(0,-189,9) rot=(0,-0.707107,0.707107;3.14159rad)
  Placement2 = pos=(1.78975,1.17e-14,0) rot=(0,0,1;0rad)
  Reference1 = -> Assembly [Body005.Face10,Body005.Vertex5]
  Reference2 = -> Assembly [KV1_45_H45_L____SC002.Junker_H45SC_op_350.Part__Feature.Face145,KV1_45_H45_L____SC002.Junker_H45SC_op_350.Part__Feature.Face145]
FEATURE [App::FeaturePython] Joint017  label="Distance016"  # Assembly joint (typed FeaturePython)
  Activated = true
  AngleMax = 0
  AngleMin = 0
  Detach1 = false
  Detach2 = false
  Distance = 0
  Distance2 = 0
  EnableAngleMax = false
  EnableAngleMin = false
  EnableLengthMax = false
  EnableLengthMin = false
  JointType = 5 (Distance)
  LengthMax = 0
  LengthMin = 0
  Placement1 = pos=(-1.2,0.000268538,-180.383) rot=(-0.57735,-0.57735,0.57735;2.0944rad)
  Placement2 = pos=(0.0538161,-6.11853,0) rot=(0,0,1;0rad)
  Reference1 = -> Assembly [KV1_45_H45_L____SC003.Junker_H45SC_op_350.Part__Feature.Face126,KV1_45_H45_L____SC003.Junker_H45SC_op_350.Part__Feature.Vertex171]
  Reference2 = -> Assembly [Body005.Face6,Body005.Vertex21]
FEATURE [App::FeaturePython] Joint018  label="Distance017"  # Assembly joint (typed FeaturePython)
  Activated = true
  AngleMax = 0
  AngleMin = 0
  Detach1 = false
  Detach2 = false
  Distance = 0.5
  Distance2 = 0
  EnableAngleMax = false
  EnableAngleMin = false
  EnableLengthMax = false
  EnableLengthMin = false
  JointType = 5 (Distance)
  LengthMax = 0
  LengthMin = 0
  Placement1 = pos=(1.78975,1.17e-14,0) rot=(0,0,1;0rad)
  Placement2 = pos=(0,-189,9) rot=(0,-0.707107,0.707107;3.14159rad)
  Reference1 = -> Assembly [KV1_45_H45_L____SC003.Junker_H45SC_op_350.Part__Feature.Face145,KV1_45_H45_L____SC003.Junker_H45SC_op_350.Part__Feature.Vertex242]
  Reference2 = -> Assembly [Body005.Face10,Body005.Face10]
FEATURE [App::FeaturePython] Joint019  label="Distance018"  # Assembly joint (typed FeaturePython)
  Activated = true
  AngleMax = 0
  AngleMin = 0
  Detach1 = false
  Detach2 = false
  Distance = 0
  Distance2 = 0
  EnableAngleMax = false
  EnableAngleMin = false
  EnableLengthMax = false
  EnableLengthMin = false
  JointType = 5 (Distance)
  LengthMax = 0
  LengthMin = 0
  Placement1 = pos=(-1.2,0.000268538,-180.383) rot=(-0.57735,-0.57735,0.57735;2.0944rad)
  Placement2 = pos=(0.0538161,-6.11853,0) rot=(0,0,1;0rad)
  Reference1 = -> Assembly [KV1_45_H45_L____SC001.Junker_H45SC_op_350.Part__Feature.Face126,KV1_45_H45_L____SC001.Junker_H45SC_op_350.Part__Feature.Edge73]
  Reference2 = -> Assembly [Body005.Face6,Body005.Vertex21]
FEATURE [App::FeaturePython] Joint020  label="Distance019"  # Assembly joint (typed FeaturePython)
  Activated = true
  AngleMax = 0
  AngleMin = 0
  Detach1 = false
  Detach2 = false
  Distance = -0.5
  Distance2 = 0
  EnableAngleMax = false
  EnableAngleMin = false
  EnableLengthMax = false
  EnableLengthMin = false
  JointType = 5 (Distance)
  LengthMax = 0
  LengthMin = 0
  Placement1 = pos=(0,-189,9) rot=(0,-0.707107,0.707107;3.14159rad)
  Placement2 = pos=(-1.2,0,0) rot=(-0.57735,-0.57735,0.57735;4.18879rad)
  Reference1 = -> Assembly [Body005.Face10,Body005.Face10]
  Reference2 = -> Assembly [KV1_45_H45_L____SC001.Junker_H45SC_op_350.Part__Feature.Edge368,KV1_45_H45_L____SC001.Junker_H45SC_op_350.Part__Feature.Vertex242]
FEATURE [App::FeaturePython] Joint021  label="Cylindrical001"  # Assembly joint (typed FeaturePython)
  Activated = true
  AngleMax = 0
  AngleMin = 0
  Detach1 = false
  Detach2 = false
  Distance = 0
  Distance2 = 0
  EnableAngleMax = false
  EnableAngleMin = false
  EnableLengthMax = false
  EnableLengthMin = false
  JointType = 2 (Cylindrical)
  LengthMax = 0
  LengthMin = 0
  Placement1 = pos=(-0.6,0,-107.5) rot=(0,1,0;1.5708rad)
  Placement2 = pos=(-257.5,-81,0) rot=(0,0,1;0rad)
  Reference1 = -> Assembly [KV1_45_H45_L____SC002.Junker_H45SC_op_350.Part__Feature.Face31,KV1_45_H45_L____SC002.Junker_H45SC_op_350.Part__Feature.Face31]
  Reference2 = -> Assembly [Body005.Face14,Body005.Edge3]
FEATURE [App::FeaturePython] Joint022  label="Cylindrical002"  # Assembly joint (typed FeaturePython)
  Activated = true
  AngleMax = 0
  AngleMin = 0
  Detach1 = false
  Detach2 = false
  Distance = 0
  Distance2 = 0
  EnableAngleMax = false
  EnableAngleMin = false
  EnableLengthMax = false
  EnableLengthMin = false
  JointType = 2 (Cylindrical)
  LengthMax = 0
  LengthMin = 0
  Placement1 = pos=(-161.5,-81,0) rot=(0,0,1;0rad)
  Placement2 = pos=(-0.6,0,-107.5) rot=(0,1,0;1.5708rad)
  Reference1 = -> Assembly [Body005.Face17,Body005.Edge3]
  Reference2 = -> Assembly [KV1_45_H45_L____SC001.Junker_H45SC_op_350.Part__Feature.Face31,KV1_45_H45_L____SC001.Junker_H45SC_op_350.Part__Feature.Face31]
FEATURE [App::FeaturePython] Joint023  label="Cylindrical003"  # Assembly joint (typed FeaturePython)
  Activated = true
  AngleMax = 0
  AngleMin = 0
  Detach1 = false
  Detach2 = false
  Distance = 0
  Distance2 = 0
  EnableAngleMax = false
  EnableAngleMin = false
  EnableLengthMax = false
  EnableLengthMin = false
  JointType = 2 (Cylindrical)
  LengthMax = 0
  LengthMin = 0
  Placement1 = pos=(-65.5,-81,0) rot=(0,0,1;0rad)
  Placement2 = pos=(-0.6,0,-107.5) rot=(0,1,0;1.5708rad)
  Reference1 = -> Assembly [Body005.Face20,Body005.Edge3]
  Reference2 = -> Assembly [KV1_45_H45_L____SC003.Junker_H45SC_op_350.Part__Feature.Face31,KV1_45_H45_L____SC003.Junker_H45SC_op_350.Part__Feature.Face31]
FEATURE [Assembly::JointGroup] Joints
  Group = -> [GroundedJoint,Joint,Joint001,Joint002,Joint003,Joint004,Joint005,Joint006,Joint007,Joint008,Joint009,Joint010,Joint011,Joint012,Joint013,Joint014,Joint015,Joint016,Joint017,Joint018,Joint019,Joint020,Joint021,Joint022,Joint023]
FEATURE [Assembly::AssemblyObject] Assembly
  Group = -> [Joints,Body,GroundedJoint,Body003,Body004,Body005,KV1_45_H45_L____SC,Body007,Joint,Joint001,Joint002,Joint003,Joint004,Joint005,Joint006,Joint007,Joint008,Joint009,Joint010,Joint011,Joint012,Joint013,Joint014,Assembly001,KV1_45_H45_L____SC001,KV1_45_H45_L____SC002,KV1_45_H45_L____SC003,Joint015,Joint016,Joint017,Joint018,Joint019,Joint020,Joint021,Joint022,Joint023]
  Origin = -> Origin
  Type = Assembly
FEATURE [TechDraw::DrawViewDimension] Dimension003
  AngleOverride = false
  Arbitrary = false
  ArbitraryTolerances = false
  BoxCorners = (2) [(-26.25,-40.35,-1e-07),(26.25,40.35,1e-07)]
  EqualTolerance = true
  ExtensionAngle = 0
  FormatSpec = %.2w
  FormatSpecOverTolerance = %+.2w
  FormatSpecUnderTolerance = %+.2w
  Inverted = false
  LineAngle = 0
  LockPosition = false
  MeasureType = 1
  OverTolerance = 0
  References2D = -> [View]
  Rotation = 0
  ScaleType = 0
  TheoreticalExact = false
  Type = 0
  UnderTolerance = 0
  X = 27.7175
  Y = -21.8
FEATURE [TechDraw::DrawViewDimension] Dimension004
  AngleOverride = false
  Arbitrary = false
  ArbitraryTolerances = false
  BoxCorners = (2) [(-26.25,-40.35,-1e-07),(26.25,40.35,1e-07)]
  EqualTolerance = true
  ExtensionAngle = 0
  FormatSpec = %.2w
  FormatSpecOverTolerance = %+.2w
  FormatSpecUnderTolerance = %+.2w
  Inverted = false
  LineAngle = 0
  LockPosition = false
  MeasureType = 1
  OverTolerance = 0
  References2D = -> [View]
  Rotation = 0
  ScaleType = 0
  TheoreticalExact = false
  Type = 1
  UnderTolerance = 0
  X = 0
  Y = -22.7337
FEATURE [TechDraw::DrawViewDimension] Dimension005
  AngleOverride = false
  Arbitrary = false
  ArbitraryTolerances = false
  BoxCorners = (2) [(-26.25,-40.35,-1e-07),(26.25,40.35,1e-07)]
  EqualTolerance = true
  ExtensionAngle = 0
  FormatSpec = %.2w
  FormatSpecOverTolerance = %+.2w
  FormatSpecUnderTolerance = %+.2w
  Inverted = false
  LineAngle = 0
  LockPosition = false
  MeasureType = 1
  OverTolerance = 0
  References2D = -> [View]
  Rotation = 0
  ScaleType = 0
  TheoreticalExact = false
  Type = 0
  UnderTolerance = 0
  X = 32.776
  Y = 7.8134
FEATURE [TechDraw::DrawViewDimension] Dimension006
  AngleOverride = false
  Arbitrary = false
  ArbitraryTolerances = false
  BoxCorners = (2) [(-19.65,-40.35,0),(19.65,40.35,0)]
  EqualTolerance = true
  ExtensionAngle = 0
  FormatSpec = %.2w
  FormatSpecOverTolerance = %+.2w
  FormatSpecUnderTolerance = %+.2w
  Inverted = false
  LineAngle = 0
  LockPosition = false
  MeasureType = 1
  OverTolerance = 0
  References2D = -> [ProjItem]
  Rotation = 0
  ScaleType = 0
  TheoreticalExact = false
  Type = 0
  UnderTolerance = 0
  X = 4.61091
  Y = -56.391
FEATURE [TechDraw::DrawPage] Page
  KeepUpdated = true
  NextBalloonIndex = 1
  ProjectionType = 0
  Template = -> Template
  Views = -> [ProjGroup,Dimension,Dimension001,Dimension002,Dimension003,Dimension004,Dimension005,Dimension006]
---- part 80_base_assembly.FCStd = doc fcstd_fe5b77038706 ----
FCSTD DOCUMENT  (FreeCAD 1.0R39109 (Git))
Label: 80_base_assembly
License: All rights reserved
LicenseURL: http://en.wikipedia.org/wiki/All_rights_reserved
objects: App::FeaturePython×10, App::Link×4, Assembly::JointGroup×1, Assembly::AssemblyObject×1
EXTERNAL_REF file=81_base_front_and_back.FCStd obj=Body
EXTERNAL_REF file=82_base_sides.FCStd obj=Body

FEATURE [App::Link] Body
  LinkedObject = -> <external 81_base_front_and_back.FCStd>#Body
FEATURE [App::FeaturePython] GroundedJoint  # Assembly grounded joint (typed FeaturePython)
  ObjectToGround = -> Body
FEATURE [App::Link] Body001
  LinkPlacement = pos=(-1.91e-14,1.232e-13,375) rot=(1,0,0;3.14159rad)
  LinkedObject = -> <external 81_base_front_and_back.FCStd>#Body
  Placement = pos=(-1.91e-14,1.232e-13,375) rot=(1,0,0;3.14159rad)
FEATURE [App::Link] Body002
  LinkPlacement = pos=(-262.5,9.58e-14,187.5) rot=(0.707107,0,0.707107;3.14159rad)
  LinkedObject = -> <external 82_base_sides.FCStd>#Body
  Placement = pos=(-262.5,9.58e-14,187.5) rot=(0.707107,0,0.707107;3.14159rad)
FEATURE [App::Link] Body003
  LinkPlacement = pos=(244.5,3.53e-14,187.5) rot=(0,1,0;1.5708rad)
  LinkedObject = -> <external 82_base_sides.FCStd>#Body
  Placement = pos=(244.5,3.53e-14,187.5) rot=(0,1,0;1.5708rad)
FEATURE [App::FeaturePython] Joint  label="s1-1"  # Assembly joint (typed FeaturePython)
  Activated = true
  AngleMax = 0
  AngleMin = 0
  Detach1 = false
  Detach2 = false
  Distance = 0
  Distance2 = 0
  EnableAngleMax = false
  EnableAngleMin = false
  EnableLengthMax = false
  EnableLengthMin = false
  JointType = 5 (Distance)
  LengthMax = 0
  LengthMin = 0
  Placement1 = pos=(169.5,1e-16,9) rot=(-0.57735,0.57735,-0.57735;2.0944rad)
  Placement2 = pos=(4.7e-15,6e-16,18) rot=(0,0,1;0rad)
  Reference1 = -> Assembly [Body003.Face2,Body003.?Vertex6]
  Reference2 = -> Assembly [Body.Face6,Body.Vertex6]
FEATURE [App::FeaturePython] Joint001  label="s1-2"  # Assembly joint (typed FeaturePython)
  Activated = true
  AngleMax = 0
  AngleMin = 0
  Detach1 = false
  Detach2 = false
  Distance = 0
  Distance2 = 0
  EnableAngleMax = false
  EnableAngleMin = false
  EnableLengthMax = false
  EnableLengthMin = false
  JointType = 5 (Distance)
  LengthMax = 0
  LengthMin = 0
  Placement1 = pos=(0,-25,9) rot=(0,-0.707107,0.707107;3.14159rad)
  Placement2 = pos=(-2e-16,-25,9) rot=(0,-0.707107,0.707107;3.14159rad)
  Reference1 = -> Assembly [Body003.Face3,Body003.Face3]
  Reference2 = -> Assembly [Body.Face3,Body.Vertex5]
FEATURE [App::FeaturePython] Joint002  label="s1-3"  # Assembly joint (typed FeaturePython)
  Activated = true
  AngleMax = 0
  AngleMin = 0
  Detach1 = false
  Detach2 = false
  Distance = 0
  Distance2 = 0
  EnableAngleMax = false
  EnableAngleMin = false
  EnableLengthMax = false
  EnableLengthMin = false
  JointType = 5 (Distance)
  LengthMax = 0
  LengthMin = 0
  Placement1 = pos=(0,2e-15,18) rot=(0,0,1;0rad)
  Placement2 = pos=(262.5,4e-16,9) rot=(0.57735,-0.57735,0.57735;4.18879rad)
  Reference1 = -> Assembly [Body003.Face6,Body003.Face6]
  Reference2 = -> Assembly [Body.Face2,Body.Face2]
FEATURE [App::FeaturePython] Joint003  label="s2-1"  # Assembly joint (typed FeaturePython)
  Activated = true
  AngleMax = 0
  AngleMin = 0
  Detach1 = false
  Detach2 = false
  Distance = 0
  Distance2 = 0
  EnableAngleMax = false
  EnableAngleMin = false
  EnableLengthMax = false
  EnableLengthMin = false
  JointType = 5 (Distance)
  LengthMax = 0
  LengthMin = 0
  Placement1 = pos=(0,25,9) rot=(-1,0,0;1.5708rad)
  Placement2 = pos=(-2e-16,-25,9) rot=(0,-0.707107,0.707107;3.14159rad)
  Reference1 = -> Assembly [Body002.Face1,Body002.Face1]
  Reference2 = -> Assembly [Body.Face3,Body.Vertex7]
FEATURE [App::FeaturePython] Joint004  label="s2-2"  # Assembly joint (typed FeaturePython)
  Activated = true
  AngleMax = 0
  AngleMin = 0
  Detach1 = false
  Detach2 = false
  Distance = 0
  Distance2 = 0
  EnableAngleMax = false
  EnableAngleMin = false
  EnableLengthMax = false
  EnableLengthMin = false
  JointType = 5 (Distance)
  LengthMax = 0
  LengthMin = 0
  Placement1 = pos=(-169.5,-6e-16,9) rot=(0.57735,0.57735,-0.57735;4.18879rad)
  Placement2 = pos=(4.7e-15,6e-16,18) rot=(0,0,1;0rad)
  Reference1 = -> Assembly [Body002.Face4,Body002.?Vertex1]
  Reference2 = -> Assembly [Body.Face6,Body.Vertex2]
FEATURE [App::FeaturePython] Joint005  label="s2-3"  # Assembly joint (typed FeaturePython)
  Activated = true
  AngleMax = 0
  AngleMin = 0
  Detach1 = false
  Detach2 = false
  Distance = 0
  Distance2 = 0
  EnableAngleMax = false
  EnableAngleMin = false
  EnableLengthMax = false
  EnableLengthMin = false
  JointType = 5 (Distance)
  LengthMax = 0
  LengthMin = 0
  Placement1 = pos=(-262.5,-4e-16,9) rot=(-0.57735,-0.57735,0.57735;2.0944rad)
  Placement2 = pos=(0,1.7e-15,0) rot=(0,0,1;0rad)
  Reference1 = -> Assembly [Body.Face4,Body.Face4]
  Reference2 = -> Assembly [Body002.Face5,Body002.?Vertex1]
FEATURE [App::FeaturePython] Joint006  label="B1-1"  # Assembly joint (typed FeaturePython)
  Activated = true
  AngleMax = 0
  AngleMin = 0
  Detach1 = false
  Detach2 = false
  Distance = 0
  Distance2 = 0
  EnableAngleMax = false
  EnableAngleMin = false
  EnableLengthMax = false
  EnableLengthMin = false
  JointType = 5 (Distance)
  LengthMax = 0
  LengthMin = 0
  Placement1 = pos=(0,2e-15,18) rot=(0,0,1;0rad)
  Placement2 = pos=(262.5,-1.3e-15,9) rot=(-0.57735,0.57735,-0.57735;2.0944rad)
  Reference1 = -> Assembly [Body003.Face6,Body003.?Vertex2]
  Reference2 = -> Assembly [Body001.Face2,Body001.Face2]
FEATURE [App::FeaturePython] Joint007  label="B1-2"  # Assembly joint (typed FeaturePython)
  Activated = true
  AngleMax = 0
  AngleMin = 0
  Detach1 = false
  Detach2 = false
  Distance = 0
  Distance2 = 0
  EnableAngleMax = false
  EnableAngleMin = false
  EnableLengthMax = false
  EnableLengthMin = false
  JointType = 5 (Distance)
  LengthMax = 0
  LengthMin = 0
  Placement1 = pos=(-6.4e-15,25,9) rot=(-1,0,0;1.5708rad)
  Placement2 = pos=(0,-25,9) rot=(0,-0.707107,0.707107;3.14159rad)
  Reference1 = -> Assembly [Body001.Face1,Body001.Vertex3]
  Reference2 = -> Assembly [Body003.Face3,Body003.?Vertex8]
FEATURE [App::FeaturePython] Joint008  label="B1-3"  # Assembly joint (typed FeaturePython)
  Activated = true
  AngleMax = 0
  AngleMin = 0
  Detach1 = false
  Detach2 = false
  Distance = 0
  Distance2 = 0
  EnableAngleMax = false
  EnableAngleMin = false
  EnableLengthMax = false
  EnableLengthMin = false
  JointType = 5 (Distance)
  LengthMax = 0
  LengthMin = 0
  Placement1 = pos=(-169.5,1e-16,9) rot=(-0.57735,-0.57735,0.57735;2.0944rad)
  Placement2 = pos=(-4e-15,1.2e-15,18) rot=(0,0,1;0rad)
  Reference1 = -> Assembly [Body003.Face4,Body003.Face4]
  Reference2 = -> Assembly [Body001.Face6,Body001.Face6]
FEATURE [Assembly::JointGroup] Joints
  Group = -> [GroundedJoint,Joint,Joint001,Joint002,Joint003,Joint004,Joint005,Joint006,Joint007,Joint008]
FEATURE [Assembly::AssemblyObject] Assembly
  Group = -> [Joints,Body,GroundedJoint,Body001,Body002,Body003,Joint,Joint001,Joint002,Joint003,Joint004,Joint005,Joint006,Joint007,Joint008]
  Origin = -> Origin
  Type = Assembly
